# Revit family: 859-001X-001 DN65-300
name_source: partatom
category: Pipe Accessories
units: mm (PartAtom-declared; Revit-internal decimal feet)

## family parameters
Always vertical = Yes
Cut with Voids When Loaded = No
Part Type = Valve - Breaks Into
Round Connector Dimension = Use Diameter
Shared = No
Work Plane-Based = No

## types (41) — shared parameters
10 = 10 mm  [stored 0.0328084 ft]
131 = 131 mm
18 = 11 mm  [stored 0.0360892 ft]
3 = 3 mm  [stored 0.00984252 ft]
48 = 15 mm  [stored 0.0492126 ft]
50 = 50 mm
53 = 20 mm  [stored 0.0656168 ft]
8 = 8 mm  [stored 0.0262467 ft]
DN100_PN10/16_Pilot range ( 0,3 - 1,5) = 859-0100-00-1140018
DN100_PN10/16_Pilot range ( 1,5 - 6) = 859-0100-00-1140010
DN100_PN10/16_Pilot range ( 10 - 16) = 859-0100-00-1140012
DN100_PN10/16_Pilot range ( 5 - 11) = 859-0100-00-1140011
DN125_PN10/16_Pilot range ( 0,3 - 1,5) = 859-0125-00-1140018
DN125_PN10/16_Pilot range ( 1,5 - 6) = 859-0125-00-1140010
DN125_PN10/16_Pilot range ( 10 - 16) = 859-0125-00-1140012
DN125_PN10/16_Pilot range ( 5 - 11) = 859-0125-00-1140011
DN150_PN10/16_Pilot range ( 0,3 - 1,5) = 859-0150-00-1140018
DN150_PN10/16_Pilot range ( 1,5 - 6) = 859-0150-00-1140010
DN150_PN10/16_Pilot range ( 10 - 16) = 859-0150-00-1140012
DN150_PN10/16_Pilot range ( 5 - 11) = 859-0150-00-1140011
DN200_PN10_Pilot range ( 0,3 - 1,5) = 859-0200-00-0140018
DN200_PN10_Pilot range ( 1,5 - 6) = 859-0200-00-0140010
DN200_PN10_Pilot range ( 5 - 10) = 859-0200-00-0140011
DN200_PN16_Pilot range ( 0,3 - 1,5) = 859-0200-00-1140018
DN200_PN16_Pilot range ( 1,5 - 6) = 859-0200-00-1140010
DN200_PN16_Pilot range ( 10 - 16) = 859-0200-00-1140012
DN200_PN16_Pilot range ( 5 - 11) = 859-0200-00-1140011
DN250_PN10_Pilot range ( 0,3 - 1,5) = 859-0250-00-0140018
DN250_PN10_Pilot range ( 1,5 - 6) = 859-0250-00-0140010
DN250_PN10_Pilot range ( 5 - 10) = 859-0250-00-0140011
DN250_PN16_Pilot range ( 0,3 - 1,5) = 859-0250-00-1140018
DN250_PN16_Pilot range ( 1,5 - 6) = 859-0250-00-1140010
DN250_PN16_Pilot range ( 10 - 16) = 859-0250-00-1140012
DN250_PN16_Pilot range ( 5 - 11) = 859-0250-00-1140011
DN300_PN10_Pilot range ( 0,3 - 1,5) = 859-0300-00-0140018
DN300_PN10_Pilot range ( 1,5 - 6) = 859-0300-00-0140010
DN300_PN10_Pilot range ( 5 - 10) = 859-0300-00-0140011
DN300_PN16_Pilot range ( 0,3 - 1,5) = 859-0300-00-1140018
DN300_PN16_Pilot range ( 1,5 - 6) = 859-0300-00-1140010
DN300_PN16_Pilot range ( 10 - 16) = 859-0300-00-1140012
DN300_PN16_Pilot range ( 5 - 11) = 859-0300-00-1140011
DN65_PN10/16_Pilot range ( 0,3 - 1,5) = 859-0065-00-1140018
DN65_PN10/16_Pilot range ( 1,5 - 6) = 859-0065-00-1140010
DN65_PN10/16_Pilot range ( 10 - 16) = 859-0065-00-1140012
DN65_PN10/16_Pilot range ( 5 - 11) = 859-0065-00-1140011
DN80_PN10/16_Pilot range ( 0,3 - 1,5) = 859-0080-00-1140018
DN80_PN10/16_Pilot range ( 1,5 - 6) = 859-0080-00-1140010
DN80_PN10/16_Pilot range ( 10 - 16) = 859-0080-00-1140012
DN80_PN10/16_Pilot range ( 5 - 11) = 859-0080-00-1140011
Description_ = AVK CONTROL VALVE, PRESSURE SUSTAINING/RELIEF, PN10/16
Search_table = 859-001X-001 DN65-300
URL_product_pages = https://www.avkvalves.com
zero-valued in all types: 0, Actuator, Default Elevation

## per-type parameters (varying)
- DN065_PN10/16_Pilot range ( 0,3 - 1,5): Actuator_L=42 mm; Actuator_L1=38 mm; Actuator_d=24 mm  [stored 0.0787402 ft]; Body_H=87 mm; Body_Rib_L=36 mm  [stored 0.11811 ft]; Bolt_Dia=20 mm  [stored 0.0656168 ft]; Bonnet_D=44 mm; Bonnet_D1=87 mm; Bonnet_R=91 mm; Bonnet_dia=94 mm; Bonnet_dim1=61 mm; Bonnet_dim1_H=46 mm; Bonnet_dim1_H1=197 mm; Bonnet_dim2=30 mm  [stored 0.0984252 ft]; Bonnet_dim3=23 mm; Bore=33 mm; Bore1=39 mm  [stored 0.127953 ft]; Bore2=52 mm; Centre_D=25 mm  [stored 0.082021 ft]; Centre_D1=20 mm  [stored 0.0656168 ft]; Centre_nut=19 mm  [stored 0.062336 ft]; Conrol_dim.=52 mm; Control_dim1=9 mm  [stored 0.0295276 ft]; Control_dim2=27 mm; Control_dim3=5 mm  [stored 0.0164042 ft]; Control_dim4=78 mm; Control_dim5=12 mm  [stored 0.0393701 ft]; Control_dim6=15 mm  [stored 0.0492126 ft]; Control_dim7=20 mm  [stored 0.0656168 ft]; D=73 mm; DN=65 mm; FL_T=19 mm  [stored 0.062336 ft]; H3=348 mm; H33=24 mm  [stored 0.0787402 ft]; H4=47 mm; L=290 mm; L3=100 mm; Nut_Dim1=25 mm  [stored 0.082021 ft]; Nut_Dim2=4 mm  [stored 0.0131234 ft]; Nut_T=15 mm  [stored 0.0492126 ft]; Raised_R=16 mm  [stored 0.0524934 ft]; Raised_dis=3 mm  [stored 0.00984252 ft]; Sweep_R=11 mm  [stored 0.0360892 ft]; Thickness=11 mm  [stored 0.0360892 ft]; Thickness1=14 mm  [stored 0.0459318 ft]; W=134 mm; W1=141 mm; W11=101 mm; W2=94 mm; W22=75 mm; Wd1=135 mm; Wd2=135 mm; centre=51 mm; dim1=56 mm; nut_dim=44 mm; sweep=18 mm  [stored 0.0590551 ft]; sweep/2=4 mm  [stored 0.0131234 ft]; sweep1=8 mm  [stored 0.0262467 ft]; sweep_2=4 mm  [stored 0.0131234 ft]; sweep_D=15 mm  [stored 0.0492126 ft]; sweep_H=179 mm; sweep_H1=64 mm; sweep_box1=16 mm  [stored 0.0524934 ft]; sweep_box2=10 mm  [stored 0.0328084 ft]
- DN065_PN10/16_Pilot range ( 1,5 - 6): Actuator_L=42 mm; Actuator_L1=38 mm; Actuator_d=24 mm  [stored 0.0787402 ft]; Body_H=87 mm; Body_Rib_L=36 mm  [stored 0.11811 ft]; Bolt_Dia=20 mm  [stored 0.0656168 ft]; Bonnet_D=44 mm; Bonnet_D1=87 mm; Bonnet_R=91 mm; Bonnet_dia=94 mm; Bonnet_dim1=61 mm; Bonnet_dim1_H=46 mm; Bonnet_dim1_H1=197 mm; Bonnet_dim2=30 mm  [stored 0.0984252 ft]; Bonnet_dim3=23 mm; Bore=33 mm; Bore1=39 mm  [stored 0.127953 ft]; Bore2=52 mm; Centre_D=25 mm  [stored 0.082021 ft]; Centre_D1=20 mm  [stored 0.0656168 ft]; Centre_nut=19 mm  [stored 0.062336 ft]; Conrol_dim.=52 mm; Control_dim1=9 mm  [stored 0.0295276 ft]; Control_dim2=27 mm; Control_dim3=5 mm  [stored 0.0164042 ft]; Control_dim4=78 mm; Control_dim5=12 mm  [stored 0.0393701 ft]; Control_dim6=15 mm  [stored 0.0492126 ft]; Control_dim7=20 mm  [stored 0.0656168 ft]; D=73 mm; DN=65 mm; FL_T=19 mm  [stored 0.062336 ft]; H3=348 mm; H33=24 mm  [stored 0.0787402 ft]; H4=47 mm; L=290 mm; L3=100 mm; Nut_Dim1=25 mm  [stored 0.082021 ft]; Nut_Dim2=4 mm  [stored 0.0131234 ft]; Nut_T=15 mm  [stored 0.0492126 ft]; Raised_R=16 mm  [stored 0.0524934 ft]; Raised_dis=3 mm  [stored 0.00984252 ft]; Sweep_R=11 mm  [stored 0.0360892 ft]; Thickness=11 mm  [stored 0.0360892 ft]; Thickness1=14 mm  [stored 0.0459318 ft]; W=134 mm; W1=141 mm; W11=101 mm; W2=94 mm; W22=75 mm; Wd1=135 mm; Wd2=135 mm; centre=51 mm; dim1=56 mm; nut_dim=44 mm; sweep=18 mm  [stored 0.0590551 ft]; sweep/2=4 mm  [stored 0.0131234 ft]; sweep1=8 mm  [stored 0.0262467 ft]; sweep_2=4 mm  [stored 0.0131234 ft]; sweep_D=15 mm  [stored 0.0492126 ft]; sweep_H=179 mm; sweep_H1=64 mm; sweep_box1=16 mm  [stored 0.0524934 ft]; sweep_box2=10 mm  [stored 0.0328084 ft]
- DN065_PN10/16_Pilot range ( 5 - 11): Actuator_L=42 mm; Actuator_L1=38 mm; Actuator_d=24 mm  [stored 0.0787402 ft]; Body_H=87 mm; Body_Rib_L=36 mm  [stored 0.11811 ft]; Bolt_Dia=20 mm  [stored 0.0656168 ft]; Bonnet_D=44 mm; Bonnet_D1=87 mm; Bonnet_R=91 mm; Bonnet_dia=94 mm; Bonnet_dim1=61 mm; Bonnet_dim1_H=46 mm; Bonnet_dim1_H1=197 mm; Bonnet_dim2=30 mm  [stored 0.0984252 ft]; Bonnet_dim3=23 mm; Bore=33 mm; Bore1=39 mm  [stored 0.127953 ft]; Bore2=52 mm; Centre_D=25 mm  [stored 0.082021 ft]; Centre_D1=20 mm  [stored 0.0656168 ft]; Centre_nut=19 mm  [stored 0.062336 ft]; Conrol_dim.=52 mm; Control_dim1=9 mm  [stored 0.0295276 ft]; Control_dim2=27 mm; Control_dim3=5 mm  [stored 0.0164042 ft]; Control_dim4=78 mm; Control_dim5=12 mm  [stored 0.0393701 ft]; Control_dim6=15 mm  [stored 0.0492126 ft]; Control_dim7=20 mm  [stored 0.0656168 ft]; D=73 mm; DN=65 mm; FL_T=19 mm  [stored 0.062336 ft]; H3=348 mm; H33=24 mm  [stored 0.0787402 ft]; H4=47 mm; L=290 mm; L3=100 mm; Nut_Dim1=25 mm  [stored 0.082021 ft]; Nut_Dim2=4 mm  [stored 0.0131234 ft]; Nut_T=15 mm  [stored 0.0492126 ft]; Raised_R=16 mm  [stored 0.0524934 ft]; Raised_dis=3 mm  [stored 0.00984252 ft]; Sweep_R=11 mm  [stored 0.0360892 ft]; Thickness=11 mm  [stored 0.0360892 ft]; Thickness1=14 mm  [stored 0.0459318 ft]; W=134 mm; W1=141 mm; W11=101 mm; W2=94 mm; W22=75 mm; Wd1=135 mm; Wd2=135 mm; centre=51 mm; dim1=56 mm; nut_dim=44 mm; sweep=18 mm  [stored 0.0590551 ft]; sweep/2=4 mm  [stored 0.0131234 ft]; sweep1=8 mm  [stored 0.0262467 ft]; sweep_2=4 mm  [stored 0.0131234 ft]; sweep_D=15 mm  [stored 0.0492126 ft]; sweep_H=179 mm; sweep_H1=64 mm; sweep_box1=16 mm  [stored 0.0524934 ft]; sweep_box2=10 mm  [stored 0.0328084 ft]
- DN065_PN10/16_Pilot range ( 10 - 16): Actuator_L=42 mm; Actuator_L1=38 mm; Actuator_d=24 mm  [stored 0.0787402 ft]; Body_H=87 mm; Body_Rib_L=36 mm  [stored 0.11811 ft]; Bolt_Dia=20 mm  [stored 0.0656168 ft]; Bonnet_D=44 mm; Bonnet_D1=87 mm; Bonnet_R=91 mm; Bonnet_dia=94 mm; Bonnet_dim1=61 mm; Bonnet_dim1_H=46 mm; Bonnet_dim1_H1=197 mm; Bonnet_dim2=30 mm  [stored 0.0984252 ft]; Bonnet_dim3=23 mm; Bore=33 mm; Bore1=39 mm  [stored 0.127953 ft]; Bore2=52 mm; Centre_D=25 mm  [stored 0.082021 ft]; Centre_D1=20 mm  [stored 0.0656168 ft]; Centre_nut=19 mm  [stored 0.062336 ft]; Conrol_dim.=52 mm; Control_dim1=9 mm  [stored 0.0295276 ft]; Control_dim2=27 mm; Control_dim3=5 mm  [stored 0.0164042 ft]; Control_dim4=78 mm; Control_dim5=12 mm  [stored 0.0393701 ft]; Control_dim6=15 mm  [stored 0.0492126 ft]; Control_dim7=20 mm  [stored 0.0656168 ft]; D=73 mm; DN=65 mm; FL_T=19 mm  [stored 0.062336 ft]; H3=348 mm; H33=24 mm  [stored 0.0787402 ft]; H4=47 mm; L=290 mm; L3=100 mm; Nut_Dim1=25 mm  [stored 0.082021 ft]; Nut_Dim2=4 mm  [stored 0.0131234 ft]; Nut_T=15 mm  [stored 0.0492126 ft]; Raised_R=16 mm  [stored 0.0524934 ft]; Raised_dis=3 mm  [stored 0.00984252 ft]; Sweep_R=11 mm  [stored 0.0360892 ft]; Thickness=11 mm  [stored 0.0360892 ft]; Thickness1=14 mm  [stored 0.0459318 ft]; W=134 mm; W1=141 mm; W11=101 mm; W2=94 mm; W22=75 mm; Wd1=135 mm; Wd2=135 mm; centre=51 mm; dim1=56 mm; nut_dim=44 mm; sweep=18 mm  [stored 0.0590551 ft]; sweep/2=4 mm  [stored 0.0131234 ft]; sweep1=8 mm  [stored 0.0262467 ft]; sweep_2=4 mm  [stored 0.0131234 ft]; sweep_D=15 mm  [stored 0.0492126 ft]; sweep_H=179 mm; sweep_H1=64 mm; sweep_box1=16 mm  [stored 0.0524934 ft]; sweep_box2=10 mm  [stored 0.0328084 ft]
- DN080_PN10/16_Pilot range ( 0,3 - 1,5): Actuator_L=49 mm; Actuator_L1=44 mm; Actuator_d=26 mm; Body_H=96 mm; Body_Rib_L=40 mm  [stored 0.131234 ft]; Bolt_Dia=20 mm  [stored 0.0656168 ft]; Bonnet_D=48 mm; Bonnet_D1=96 mm; Bonnet_R=101 mm; Bonnet_dia=108 mm; Bonnet_dim1=67 mm; Bonnet_dim1_H=45 mm; Bonnet_dim1_H1=205 mm; Bonnet_dim2=34 mm; Bonnet_dim3=25 mm  [stored 0.082021 ft]; Bore=40 mm  [stored 0.131234 ft]; Bore1=48 mm; Bore2=64 mm; Centre_D=25 mm  [stored 0.082021 ft]; Centre_D1=20 mm  [stored 0.0656168 ft]; Centre_nut=19 mm  [stored 0.062336 ft]; Conrol_dim.=57 mm; Control_dim1=10 mm  [stored 0.0328084 ft]; Control_dim2=30 mm  [stored 0.0984252 ft]; Control_dim3=5 mm  [stored 0.0164042 ft]; Control_dim4=86 mm; Control_dim5=14 mm  [stored 0.0459318 ft]; Control_dim6=16 mm  [stored 0.0524934 ft]; Control_dim7=22 mm  [stored 0.0721785 ft]; D=80 mm; DN=80 mm; FL_T=19 mm  [stored 0.062336 ft]; H3=367 mm; H33=25 mm  [stored 0.082021 ft]; H4=49 mm; L=310 mm; L3=111 mm; Nut_Dim1=25 mm  [stored 0.082021 ft]; Nut_Dim2=4 mm  [stored 0.0131234 ft]; Nut_T=15 mm  [stored 0.0492126 ft]; Raised_R=16 mm  [stored 0.0524934 ft]; Raised_dis=3 mm  [stored 0.00984252 ft]; Sweep_R=11 mm  [stored 0.0360892 ft]; Thickness=11 mm  [stored 0.0360892 ft]; Thickness1=14 mm  [stored 0.0459318 ft]; W=134 mm; W1=141 mm; W11=101 mm; W2=108 mm; W22=86 mm; Wd1=135 mm; Wd2=135 mm; centre=62 mm; dim1=56 mm; nut_dim=48 mm; sweep=18 mm  [stored 0.0590551 ft]; sweep/2=4 mm  [stored 0.0131234 ft]; sweep1=8 mm  [stored 0.0262467 ft]; sweep_2=4 mm  [stored 0.0131234 ft]; sweep_D=15 mm  [stored 0.0492126 ft]; sweep_H=187 mm; sweep_H1=63 mm; sweep_box1=16 mm  [stored 0.0524934 ft]; sweep_box2=10 mm  [stored 0.0328084 ft]
- DN080_PN10/16_Pilot range ( 1,5 - 6): Actuator_L=49 mm; Actuator_L1=44 mm; Actuator_d=26 mm; Body_H=96 mm; Body_Rib_L=40 mm  [stored 0.131234 ft]; Bolt_Dia=20 mm  [stored 0.0656168 ft]; Bonnet_D=48 mm; Bonnet_D1=96 mm; Bonnet_R=101 mm; Bonnet_dia=108 mm; Bonnet_dim1=67 mm; Bonnet_dim1_H=45 mm; Bonnet_dim1_H1=205 mm; Bonnet_dim2=34 mm; Bonnet_dim3=25 mm  [stored 0.082021 ft]; Bore=40 mm  [stored 0.131234 ft]; Bore1=48 mm; Bore2=64 mm; Centre_D=25 mm  [stored 0.082021 ft]; Centre_D1=20 mm  [stored 0.0656168 ft]; Centre_nut=19 mm  [stored 0.062336 ft]; Conrol_dim.=57 mm; Control_dim1=10 mm  [stored 0.0328084 ft]; Control_dim2=30 mm  [stored 0.0984252 ft]; Control_dim3=5 mm  [stored 0.0164042 ft]; Control_dim4=86 mm; Control_dim5=14 mm  [stored 0.0459318 ft]; Control_dim6=16 mm  [stored 0.0524934 ft]; Control_dim7=22 mm  [stored 0.0721785 ft]; D=80 mm; DN=80 mm; FL_T=19 mm  [stored 0.062336 ft]; H3=367 mm; H33=25 mm  [stored 0.082021 ft]; H4=49 mm; L=310 mm; L3=111 mm; Nut_Dim1=25 mm  [stored 0.082021 ft]; Nut_Dim2=4 mm  [stored 0.0131234 ft]; Nut_T=15 mm  [stored 0.0492126 ft]; Raised_R=16 mm  [stored 0.0524934 ft]; Raised_dis=3 mm  [stored 0.00984252 ft]; Sweep_R=11 mm  [stored 0.0360892 ft]; Thickness=11 mm  [stored 0.0360892 ft]; Thickness1=14 mm  [stored 0.0459318 ft]; W=134 mm; W1=141 mm; W11=101 mm; W2=108 mm; W22=86 mm; Wd1=135 mm; Wd2=135 mm; centre=63 mm; dim1=56 mm; nut_dim=48 mm; sweep=18 mm  [stored 0.0590551 ft]; sweep/2=4 mm  [stored 0.0131234 ft]; sweep1=8 mm  [stored 0.0262467 ft]; sweep_2=4 mm  [stored 0.0131234 ft]; sweep_D=15 mm  [stored 0.0492126 ft]; sweep_H=187 mm; sweep_H1=63 mm; sweep_box1=16 mm  [stored 0.0524934 ft]; sweep_box2=10 mm  [stored 0.0328084 ft]
- DN080_PN10/16_Pilot range ( 5 - 11): Actuator_L=49 mm; Actuator_L1=44 mm; Actuator_d=26 mm; Body_H=96 mm; Body_Rib_L=40 mm  [stored 0.131234 ft]; Bolt_Dia=20 mm  [stored 0.0656168 ft]; Bonnet_D=48 mm; Bonnet_D1=96 mm; Bonnet_R=101 mm; Bonnet_dia=108 mm; Bonnet_dim1=67 mm; Bonnet_dim1_H=45 mm; Bonnet_dim1_H1=205 mm; Bonnet_dim2=34 mm; Bonnet_dim3=25 mm  [stored 0.082021 ft]; Bore=40 mm  [stored 0.131234 ft]; Bore1=48 mm; Bore2=64 mm; Centre_D=25 mm  [stored 0.082021 ft]; Centre_D1=20 mm  [stored 0.0656168 ft]; Centre_nut=19 mm  [stored 0.062336 ft]; Conrol_dim.=57 mm; Control_dim1=10 mm  [stored 0.0328084 ft]; Control_dim2=30 mm  [stored 0.0984252 ft]; Control_dim3=5 mm  [stored 0.0164042 ft]; Control_dim4=86 mm; Control_dim5=14 mm  [stored 0.0459318 ft]; Control_dim6=16 mm  [stored 0.0524934 ft]; Control_dim7=22 mm  [stored 0.0721785 ft]; D=80 mm; DN=80 mm; FL_T=19 mm  [stored 0.062336 ft]; H3=367 mm; H33=25 mm  [stored 0.082021 ft]; H4=49 mm; L=310 mm; L3=111 mm; Nut_Dim1=25 mm  [stored 0.082021 ft]; Nut_Dim2=4 mm  [stored 0.0131234 ft]; Nut_T=15 mm  [stored 0.0492126 ft]; Raised_R=16 mm  [stored 0.0524934 ft]; Raised_dis=3 mm  [stored 0.00984252 ft]; Sweep_R=11 mm  [stored 0.0360892 ft]; Thickness=11 mm  [stored 0.0360892 ft]; Thickness1=14 mm  [stored 0.0459318 ft]; W=134 mm; W1=141 mm; W11=101 mm; W2=108 mm; W22=86 mm; Wd1=135 mm; Wd2=135 mm; centre=63 mm; dim1=56 mm; nut_dim=48 mm; sweep=18 mm  [stored 0.0590551 ft]; sweep/2=4 mm  [stored 0.0131234 ft]; sweep1=8 mm  [stored 0.0262467 ft]; sweep_2=4 mm  [stored 0.0131234 ft]; sweep_D=15 mm  [stored 0.0492126 ft]; sweep_H=187 mm; sweep_H1=63 mm; sweep_box1=16 mm  [stored 0.0524934 ft]; sweep_box2=10 mm  [stored 0.0328084 ft]
- DN080_PN10/16_Pilot range ( 10 - 16): Actuator_L=49 mm; Actuator_L1=44 mm; Actuator_d=26 mm; Body_H=96 mm; Body_Rib_L=40 mm  [stored 0.131234 ft]; Bolt_Dia=20 mm  [stored 0.0656168 ft]; Bonnet_D=48 mm; Bonnet_D1=96 mm; Bonnet_R=101 mm; Bonnet_dia=108 mm; Bonnet_dim1=67 mm; Bonnet_dim1_H=45 mm; Bonnet_dim1_H1=205 mm; Bonnet_dim2=34 mm; Bonnet_dim3=25 mm  [stored 0.082021 ft]; Bore=40 mm  [stored 0.131234 ft]; Bore1=48 mm; Bore2=64 mm; Centre_D=25 mm  [stored 0.082021 ft]; Centre_D1=20 mm  [stored 0.0656168 ft]; Centre_nut=19 mm  [stored 0.062336 ft]; Conrol_dim.=57 mm; Control_dim1=10 mm  [stored 0.0328084 ft]; Control_dim2=30 mm  [stored 0.0984252 ft]; Control_dim3=5 mm  [stored 0.0164042 ft]; Control_dim4=86 mm; Control_dim5=14 mm  [stored 0.0459318 ft]; Control_dim6=16 mm  [stored 0.0524934 ft]; Control_dim7=22 mm  [stored 0.0721785 ft]; D=80 mm; DN=80 mm; FL_T=19 mm  [stored 0.062336 ft]; H3=367 mm; H33=25 mm  [stored 0.082021 ft]; H4=49 mm; L=310 mm; L3=111 mm; Nut_Dim1=25 mm  [stored 0.082021 ft]; Nut_Dim2=4 mm  [stored 0.0131234 ft]; Nut_T=15 mm  [stored 0.0492126 ft]; Raised_R=16 mm  [stored 0.0524934 ft]; Raised_dis=3 mm  [stored 0.00984252 ft]; Sweep_R=11 mm  [stored 0.0360892 ft]; Thickness=11 mm  [stored 0.0360892 ft]; Thickness1=14 mm  [stored 0.0459318 ft]; W=134 mm; W1=141 mm; W11=101 mm; W2=108 mm; W22=86 mm; Wd1=135 mm; Wd2=135 mm; centre=63 mm; dim1=56 mm; nut_dim=48 mm; sweep=18 mm  [stored 0.0590551 ft]; sweep/2=4 mm  [stored 0.0131234 ft]; sweep1=8 mm  [stored 0.0262467 ft]; sweep_2=4 mm  [stored 0.0131234 ft]; sweep_D=15 mm  [stored 0.0492126 ft]; sweep_H=187 mm; sweep_H1=63 mm; sweep_box1=16 mm  [stored 0.0524934 ft]; sweep_box2=10 mm  [stored 0.0328084 ft]
- DN100_PN10/16_Pilot range ( 0,3 - 1,5): Actuator_L=53 mm; Actuator_L1=48 mm; Actuator_d=30 mm  [stored 0.0984252 ft]; Body_H=108 mm; Body_Rib_L=45 mm; Bolt_Dia=20 mm  [stored 0.0656168 ft]; Bonnet_D=54 mm; Bonnet_D1=108 mm; Bonnet_R=113 mm; Bonnet_dia=117 mm; Bonnet_dim1=76 mm; Bonnet_dim1_H=42 mm; Bonnet_dim1_H1=212 mm; Bonnet_dim2=38 mm; Bonnet_dim3=28 mm; Bore=50 mm; Bore1=60 mm; Bore2=80 mm; Centre_D=30 mm  [stored 0.0984252 ft]; Centre_D1=24 mm  [stored 0.0787402 ft]; Centre_nut=23 mm; Conrol_dim.=64 mm; Control_dim1=11 mm  [stored 0.0360892 ft]; Control_dim2=34 mm; Control_dim3=6 mm  [stored 0.019685 ft]; Control_dim4=97 mm; Control_dim5=15 mm  [stored 0.0492126 ft]; Control_dim6=18 mm  [stored 0.0590551 ft]; Control_dim7=25 mm  [stored 0.082021 ft]; D=90 mm; DN=100 mm; FL_T=19 mm  [stored 0.062336 ft]; H3=386 mm; H33=25 mm  [stored 0.082021 ft]; H4=51 mm; L=350 mm; L3=125 mm; Nut_Dim1=25 mm  [stored 0.082021 ft]; Nut_Dim2=5 mm  [stored 0.0164042 ft]; Nut_T=15 mm  [stored 0.0492126 ft]; Raised_R=16 mm  [stored 0.0524934 ft]; Raised_dis=3 mm  [stored 0.00984252 ft]; Sweep_R=11 mm  [stored 0.0360892 ft]; Thickness=11 mm  [stored 0.0360892 ft]; Thickness1=14 mm  [stored 0.0459318 ft]; W=134 mm; W1=141 mm; W11=101 mm; W2=118 mm; W22=94 mm; Wd1=135 mm; Wd2=138 mm; centre=78 mm; dim1=56 mm; nut_dim=54 mm; sweep=18 mm  [stored 0.0590551 ft]; sweep/2=4 mm  [stored 0.0131234 ft]; sweep1=8 mm  [stored 0.0262467 ft]; sweep_2=4 mm  [stored 0.0131234 ft]; sweep_D=15 mm  [stored 0.0492126 ft]; sweep_H=192 mm; sweep_H1=59 mm; sweep_box1=20 mm  [stored 0.0656168 ft]; sweep_box2=10 mm  [stored 0.0328084 ft]
- DN100_PN10/16_Pilot range ( 1,5 - 6): Actuator_L=53 mm; Actuator_L1=48 mm; Actuator_d=30 mm  [stored 0.0984252 ft]; Body_H=108 mm; Body_Rib_L=45 mm; Bolt_Dia=20 mm  [stored 0.0656168 ft]; Bonnet_D=54 mm; Bonnet_D1=108 mm; Bonnet_R=113 mm; Bonnet_dia=117 mm; Bonnet_dim1=76 mm; Bonnet_dim1_H=42 mm; Bonnet_dim1_H1=212 mm; Bonnet_dim2=38 mm; Bonnet_dim3=28 mm; Bore=50 mm; Bore1=60 mm; Bore2=80 mm; Centre_D=30 mm  [stored 0.0984252 ft]; Centre_D1=24 mm  [stored 0.0787402 ft]; Centre_nut=23 mm; Conrol_dim.=64 mm; Control_dim1=11 mm  [stored 0.0360892 ft]; Control_dim2=34 mm; Control_dim3=6 mm  [stored 0.019685 ft]; Control_dim4=97 mm; Control_dim5=15 mm  [stored 0.0492126 ft]; Control_dim6=18 mm  [stored 0.0590551 ft]; Control_dim7=25 mm  [stored 0.082021 ft]; D=90 mm; DN=100 mm; FL_T=19 mm  [stored 0.062336 ft]; H3=386 mm; H33=25 mm  [stored 0.082021 ft]; H4=51 mm; L=350 mm; L3=125 mm; Nut_Dim1=25 mm  [stored 0.082021 ft]; Nut_Dim2=5 mm  [stored 0.0164042 ft]; Nut_T=15 mm  [stored 0.0492126 ft]; Raised_R=16 mm  [stored 0.0524934 ft]; Raised_dis=3 mm  [stored 0.00984252 ft]; Sweep_R=11 mm  [stored 0.0360892 ft]; Thickness=11 mm  [stored 0.0360892 ft]; Thickness1=14 mm  [stored 0.0459318 ft]; W=134 mm; W1=141 mm; W11=101 mm; W2=118 mm; W22=94 mm; Wd1=135 mm; Wd2=138 mm; centre=78 mm; dim1=56 mm; nut_dim=54 mm; sweep=18 mm  [stored 0.0590551 ft]; sweep/2=4 mm  [stored 0.0131234 ft]; sweep1=8 mm  [stored 0.0262467 ft]; sweep_2=4 mm  [stored 0.0131234 ft]; sweep_D=15 mm  [stored 0.0492126 ft]; sweep_H=192 mm; sweep_H1=59 mm; sweep_box1=20 mm  [stored 0.0656168 ft]; sweep_box2=10 mm  [stored 0.0328084 ft]
- DN100_PN10/16_Pilot range ( 5 - 11): Actuator_L=53 mm; Actuator_L1=48 mm; Actuator_d=30 mm  [stored 0.0984252 ft]; Body_H=108 mm; Body_Rib_L=45 mm; Bolt_Dia=20 mm  [stored 0.0656168 ft]; Bonnet_D=54 mm; Bonnet_D1=108 mm; Bonnet_R=113 mm; Bonnet_dia=117 mm; Bonnet_dim1=76 mm; Bonnet_dim1_H=42 mm; Bonnet_dim1_H1=212 mm; Bonnet_dim2=38 mm; Bonnet_dim3=28 mm; Bore=50 mm; Bore1=60 mm; Bore2=80 mm; Centre_D=30 mm  [stored 0.0984252 ft]; Centre_D1=24 mm  [stored 0.0787402 ft]; Centre_nut=23 mm; Conrol_dim.=64 mm; Control_dim1=11 mm  [stored 0.0360892 ft]; Control_dim2=34 mm; Control_dim3=6 mm  [stored 0.019685 ft]; Control_dim4=97 mm; Control_dim5=15 mm  [stored 0.0492126 ft]; Control_dim6=18 mm  [stored 0.0590551 ft]; Control_dim7=25 mm  [stored 0.082021 ft]; D=90 mm; DN=100 mm; FL_T=19 mm  [stored 0.062336 ft]; H3=386 mm; H33=25 mm  [stored 0.082021 ft]; H4=51 mm; L=350 mm; L3=125 mm; Nut_Dim1=25 mm  [stored 0.082021 ft]; Nut_Dim2=5 mm  [stored 0.0164042 ft]; Nut_T=15 mm  [stored 0.0492126 ft]; Raised_R=16 mm  [stored 0.0524934 ft]; Raised_dis=3 mm  [stored 0.00984252 ft]; Sweep_R=11 mm  [stored 0.0360892 ft]; Thickness=11 mm  [stored 0.0360892 ft]; Thickness1=14 mm  [stored 0.0459318 ft]; W=134 mm; W1=141 mm; W11=101 mm; W2=118 mm; W22=94 mm; Wd1=135 mm; Wd2=138 mm; centre=78 mm; dim1=56 mm; nut_dim=54 mm; sweep=18 mm  [stored 0.0590551 ft]; sweep/2=4 mm  [stored 0.0131234 ft]; sweep1=8 mm  [stored 0.0262467 ft]; sweep_2=4 mm  [stored 0.0131234 ft]; sweep_D=15 mm  [stored 0.0492126 ft]; sweep_H=192 mm; sweep_H1=59 mm; sweep_box1=20 mm  [stored 0.0656168 ft]; sweep_box2=10 mm  [stored 0.0328084 ft]
- DN100_PN10/16_Pilot range ( 10 - 16): Actuator_L=53 mm; Actuator_L1=48 mm; Actuator_d=30 mm  [stored 0.0984252 ft]; Body_H=108 mm; Body_Rib_L=45 mm; Bolt_Dia=20 mm  [stored 0.0656168 ft]; Bonnet_D=54 mm; Bonnet_D1=108 mm; Bonnet_R=113 mm; Bonnet_dia=117 mm; Bonnet_dim1=76 mm; Bonnet_dim1_H=42 mm; Bonnet_dim1_H1=212 mm; Bonnet_dim2=38 mm; Bonnet_dim3=28 mm; Bore=50 mm; Bore1=60 mm; Bore2=80 mm; Centre_D=30 mm  [stored 0.0984252 ft]; Centre_D1=24 mm  [stored 0.0787402 ft]; Centre_nut=23 mm; Conrol_dim.=64 mm; Control_dim1=11 mm  [stored 0.0360892 ft]; Control_dim2=34 mm; Control_dim3=6 mm  [stored 0.019685 ft]; Control_dim4=97 mm; Control_dim5=15 mm  [stored 0.0492126 ft]; Control_dim6=18 mm  [stored 0.0590551 ft]; Control_dim7=25 mm  [stored 0.082021 ft]; D=90 mm; DN=100 mm; FL_T=19 mm  [stored 0.062336 ft]; H3=386 mm; H33=25 mm  [stored 0.082021 ft]; H4=51 mm; L=350 mm; L3=125 mm; Nut_Dim1=25 mm  [stored 0.082021 ft]; Nut_Dim2=5 mm  [stored 0.0164042 ft]; Nut_T=15 mm  [stored 0.0492126 ft]; Raised_R=16 mm  [stored 0.0524934 ft]; Raised_dis=3 mm  [stored 0.00984252 ft]; Sweep_R=11 mm  [stored 0.0360892 ft]; Thickness=11 mm  [stored 0.0360892 ft]; Thickness1=14 mm  [stored 0.0459318 ft]; W=134 mm; W1=141 mm; W11=101 mm; W2=118 mm; W22=94 mm; Wd1=135 mm; Wd2=138 mm; centre=78 mm; dim1=56 mm; nut_dim=54 mm; sweep=18 mm  [stored 0.0590551 ft]; sweep/2=4 mm  [stored 0.0131234 ft]; sweep1=8 mm  [stored 0.0262467 ft]; sweep_2=4 mm  [stored 0.0131234 ft]; sweep_D=15 mm  [stored 0.0492126 ft]; sweep_H=192 mm; sweep_H1=59 mm; sweep_box1=20 mm  [stored 0.0656168 ft]; sweep_box2=10 mm  [stored 0.0328084 ft]
- DN125_PN10/16_Pilot range ( 0,3 - 1,5): Actuator_L=53 mm; Actuator_L1=48 mm; Actuator_d=35 mm  [stored 0.114829 ft]; Body_H=126 mm; Body_Rib_L=53 mm; Bolt_Dia=20 mm  [stored 0.0656168 ft]; Bonnet_D=63 mm; Bonnet_D1=126 mm; Bonnet_R=132 mm; Bonnet_dia=117 mm; Bonnet_dim1=88 mm; Bonnet_dim1_H=35 mm  [stored 0.114829 ft]; Bonnet_dim1_H1=215 mm; Bonnet_dim2=44 mm; Bonnet_dim3=33 mm; Bore=63 mm; Bore1=75 mm; Bore2=100 mm; Centre_D=30 mm  [stored 0.0984252 ft]; Centre_D1=24 mm  [stored 0.0787402 ft]; Centre_nut=23 mm; Conrol_dim.=75 mm; Control_dim1=13 mm  [stored 0.0426509 ft]; Control_dim2=40 mm  [stored 0.131234 ft]; Control_dim3=7 mm  [stored 0.0229659 ft]; Control_dim4=113 mm; Control_dim5=18 mm  [stored 0.0590551 ft]; Control_dim6=21 mm  [stored 0.0688976 ft]; Control_dim7=29 mm; D=105 mm; DN=125 mm; FL_T=19 mm  [stored 0.062336 ft]; H3=405 mm; H33=26 mm; H4=51 mm; L=400 mm; L3=146 mm; Nut_Dim1=25 mm  [stored 0.082021 ft]; Nut_Dim2=5 mm  [stored 0.0164042 ft]; Nut_T=15 mm  [stored 0.0492126 ft]; Raised_R=17 mm; Raised_dis=3 mm  [stored 0.00984252 ft]; Sweep_R=11 mm  [stored 0.0360892 ft]; Thickness=11 mm  [stored 0.0360892 ft]; Thickness1=14 mm  [stored 0.0459318 ft]; W=134 mm; W1=141 mm; W11=101 mm; W2=118 mm; W22=94 mm; Wd1=135 mm; Wd2=148 mm; centre=98 mm; dim1=56 mm; nut_dim=63 mm; sweep=18 mm  [stored 0.0590551 ft]; sweep/2=4 mm  [stored 0.0131234 ft]; sweep1=8 mm  [stored 0.0262467 ft]; sweep_2=4 mm  [stored 0.0131234 ft]; sweep_D=15 mm  [stored 0.0492126 ft]; sweep_H=195 mm; sweep_H1=48 mm; sweep_box1=20 mm  [stored 0.0656168 ft]; sweep_box2=10 mm  [stored 0.0328084 ft]
- DN125_PN10/16_Pilot range ( 1,5 - 6): Actuator_L=53 mm; Actuator_L1=48 mm; Actuator_d=35 mm  [stored 0.114829 ft]; Body_H=126 mm; Body_Rib_L=53 mm; Bolt_Dia=20 mm  [stored 0.0656168 ft]; Bonnet_D=63 mm; Bonnet_D1=126 mm; Bonnet_R=132 mm; Bonnet_dia=117 mm; Bonnet_dim1=88 mm; Bonnet_dim1_H=35 mm  [stored 0.114829 ft]; Bonnet_dim1_H1=215 mm; Bonnet_dim2=44 mm; Bonnet_dim3=33 mm; Bore=63 mm; Bore1=75 mm; Bore2=100 mm; Centre_D=30 mm  [stored 0.0984252 ft]; Centre_D1=24 mm  [stored 0.0787402 ft]; Centre_nut=23 mm; Conrol_dim.=75 mm; Control_dim1=13 mm  [stored 0.0426509 ft]; Control_dim2=40 mm  [stored 0.131234 ft]; Control_dim3=7 mm  [stored 0.0229659 ft]; Control_dim4=113 mm; Control_dim5=18 mm  [stored 0.0590551 ft]; Control_dim6=21 mm  [stored 0.0688976 ft]; Control_dim7=29 mm; D=105 mm; DN=125 mm; FL_T=19 mm  [stored 0.062336 ft]; H3=405 mm; H33=26 mm; H4=51 mm; L=400 mm; L3=146 mm; Nut_Dim1=25 mm  [stored 0.082021 ft]; Nut_Dim2=5 mm  [stored 0.0164042 ft]; Nut_T=15 mm  [stored 0.0492126 ft]; Raised_R=17 mm; Raised_dis=3 mm  [stored 0.00984252 ft]; Sweep_R=11 mm  [stored 0.0360892 ft]; Thickness=11 mm  [stored 0.0360892 ft]; Thickness1=14 mm  [stored 0.0459318 ft]; W=134 mm; W1=141 mm; W11=101 mm; W2=118 mm; W22=94 mm; Wd1=135 mm; Wd2=148 mm; centre=98 mm; dim1=56 mm; nut_dim=63 mm; sweep=18 mm  [stored 0.0590551 ft]; sweep/2=4 mm  [stored 0.0131234 ft]; sweep1=8 mm  [stored 0.0262467 ft]; sweep_2=4 mm  [stored 0.0131234 ft]; sweep_D=15 mm  [stored 0.0492126 ft]; sweep_H=195 mm; sweep_H1=48 mm; sweep_box1=20 mm  [stored 0.0656168 ft]; sweep_box2=10 mm  [stored 0.0328084 ft]
- DN125_PN10/16_Pilot range ( 5 - 11): Actuator_L=53 mm; Actuator_L1=48 mm; Actuator_d=35 mm  [stored 0.114829 ft]; Body_H=126 mm; Body_Rib_L=53 mm; Bolt_Dia=20 mm  [stored 0.0656168 ft]; Bonnet_D=63 mm; Bonnet_D1=126 mm; Bonnet_R=132 mm; Bonnet_dia=117 mm; Bonnet_dim1=88 mm; Bonnet_dim1_H=35 mm  [stored 0.114829 ft]; Bonnet_dim1_H1=215 mm; Bonnet_dim2=44 mm; Bonnet_dim3=33 mm; Bore=63 mm; Bore1=75 mm; Bore2=100 mm; Centre_D=30 mm  [stored 0.0984252 ft]; Centre_D1=24 mm  [stored 0.0787402 ft]; Centre_nut=23 mm; Conrol_dim.=75 mm; Control_dim1=13 mm  [stored 0.0426509 ft]; Control_dim2=40 mm  [stored 0.131234 ft]; Control_dim3=7 mm  [stored 0.0229659 ft]; Control_dim4=113 mm; Control_dim5=18 mm  [stored 0.0590551 ft]; Control_dim6=21 mm  [stored 0.0688976 ft]; Control_dim7=29 mm; D=105 mm; DN=125 mm; FL_T=19 mm  [stored 0.062336 ft]; H3=405 mm; H33=26 mm; H4=51 mm; L=400 mm; L3=146 mm; Nut_Dim1=25 mm  [stored 0.082021 ft]; Nut_Dim2=5 mm  [stored 0.0164042 ft]; Nut_T=15 mm  [stored 0.0492126 ft]; Raised_R=17 mm; Raised_dis=3 mm  [stored 0.00984252 ft]; Sweep_R=11 mm  [stored 0.0360892 ft]; Thickness=11 mm  [stored 0.0360892 ft]; Thickness1=14 mm  [stored 0.0459318 ft]; W=134 mm; W1=141 mm; W11=101 mm; W2=118 mm; W22=94 mm; Wd1=135 mm; Wd2=148 mm; centre=98 mm; dim1=56 mm; nut_dim=63 mm; sweep=18 mm  [stored 0.0590551 ft]; sweep/2=4 mm  [stored 0.0131234 ft]; sweep1=8 mm  [stored 0.0262467 ft]; sweep_2=4 mm  [stored 0.0131234 ft]; sweep_D=15 mm  [stored 0.0492126 ft]; sweep_H=195 mm; sweep_H1=48 mm; sweep_box1=20 mm  [stored 0.0656168 ft]; sweep_box2=10 mm  [stored 0.0328084 ft]
- DN125_PN10/16_Pilot range ( 10 - 16): Actuator_L=53 mm; Actuator_L1=48 mm; Actuator_d=35 mm  [stored 0.114829 ft]; Body_H=126 mm; Body_Rib_L=53 mm; Bolt_Dia=20 mm  [stored 0.0656168 ft]; Bonnet_D=63 mm; Bonnet_D1=126 mm; Bonnet_R=132 mm; Bonnet_dia=117 mm; Bonnet_dim1=88 mm; Bonnet_dim1_H=35 mm  [stored 0.114829 ft]; Bonnet_dim1_H1=215 mm; Bonnet_dim2=44 mm; Bonnet_dim3=33 mm; Bore=63 mm; Bore1=75 mm; Bore2=100 mm; Centre_D=30 mm  [stored 0.0984252 ft]; Centre_D1=24 mm  [stored 0.0787402 ft]; Centre_nut=23 mm; Conrol_dim.=75 mm; Control_dim1=13 mm  [stored 0.0426509 ft]; Control_dim2=40 mm  [stored 0.131234 ft]; Control_dim3=7 mm  [stored 0.0229659 ft]; Control_dim4=113 mm; Control_dim5=18 mm  [stored 0.0590551 ft]; Control_dim6=21 mm  [stored 0.0688976 ft]; Control_dim7=29 mm; D=105 mm; DN=125 mm; FL_T=19 mm  [stored 0.062336 ft]; H3=405 mm; H33=26 mm; H4=51 mm; L=400 mm; L3=146 mm; Nut_Dim1=25 mm  [stored 0.082021 ft]; Nut_Dim2=5 mm  [stored 0.0164042 ft]; Nut_T=15 mm  [stored 0.0492126 ft]; Raised_R=17 mm; Raised_dis=3 mm  [stored 0.00984252 ft]; Sweep_R=11 mm  [stored 0.0360892 ft]; Thickness=11 mm  [stored 0.0360892 ft]; Thickness1=14 mm  [stored 0.0459318 ft]; W=134 mm; W1=141 mm; W11=101 mm; W2=118 mm; W22=94 mm; Wd1=135 mm; Wd2=148 mm; centre=98 mm; dim1=56 mm; nut_dim=63 mm; sweep=18 mm  [stored 0.0590551 ft]; sweep/2=4 mm  [stored 0.0131234 ft]; sweep1=8 mm  [stored 0.0262467 ft]; sweep_2=4 mm  [stored 0.0131234 ft]; sweep_D=15 mm  [stored 0.0492126 ft]; sweep_H=195 mm; sweep_H1=48 mm; sweep_box1=20 mm  [stored 0.0656168 ft]; sweep_box2=10 mm  [stored 0.0328084 ft]
- DN150_PN10/16_Pilot range ( 0,3 - 1,5): Actuator_L=63 mm; Actuator_L1=57 mm; Actuator_d=40 mm  [stored 0.131234 ft]; Body_H=144 mm; Body_Rib_L=60 mm; Bolt_Dia=20 mm  [stored 0.0656168 ft]; Bonnet_D=72 mm; Bonnet_D1=144 mm; Bonnet_R=151 mm; Bonnet_dia=140 mm; Bonnet_dim1=101 mm; Bonnet_dim1_H=33 mm; Bonnet_dim1_H1=231 mm; Bonnet_dim2=50 mm; Bonnet_dim3=38 mm; Bore=75 mm; Bore1=90 mm; Bore2=120 mm; Centre_D=40 mm  [stored 0.131234 ft]; Centre_D1=32 mm  [stored 0.104987 ft]; Centre_nut=30 mm  [stored 0.0984252 ft]; Conrol_dim.=86 mm; Control_dim1=15 mm  [stored 0.0492126 ft]; Control_dim2=45 mm; Control_dim3=8 mm  [stored 0.0262467 ft]; Control_dim4=130 mm; Control_dim5=20 mm  [stored 0.0656168 ft]; Control_dim6=24 mm  [stored 0.0787402 ft]; Control_dim7=33 mm; D=120 mm; DN=150 mm; FL_T=19 mm  [stored 0.062336 ft]; H3=443 mm; H33=28 mm; H4=55 mm; L=480 mm; L3=166 mm; Nut_Dim1=25 mm  [stored 0.082021 ft]; Nut_Dim2=6 mm  [stored 0.019685 ft]; Nut_T=15 mm  [stored 0.0492126 ft]; Raised_R=18 mm  [stored 0.0590551 ft]; Raised_dis=3 mm  [stored 0.00984252 ft]; Sweep_R=11 mm  [stored 0.0360892 ft]; Thickness=11 mm  [stored 0.0360892 ft]; Thickness1=14 mm  [stored 0.0459318 ft]; W=134 mm; W1=141 mm; W11=101 mm; W2=140 mm; W22=112 mm; Wd1=135 mm; Wd2=165 mm; centre=117 mm; dim1=56 mm; nut_dim=72 mm; sweep=18 mm  [stored 0.0590551 ft]; sweep/2=4 mm  [stored 0.0131234 ft]; sweep1=8 mm  [stored 0.0262467 ft]; sweep_2=4 mm  [stored 0.0131234 ft]; sweep_D=15 mm  [stored 0.0492126 ft]; sweep_H=210 mm; sweep_H1=46 mm; sweep_box1=26 mm; sweep_box2=10 mm  [stored 0.0328084 ft]
- DN150_PN10/16_Pilot range ( 1,5 - 6): Actuator_L=63 mm; Actuator_L1=57 mm; Actuator_d=40 mm  [stored 0.131234 ft]; Body_H=144 mm; Body_Rib_L=60 mm; Bolt_Dia=20 mm  [stored 0.0656168 ft]; Bonnet_D=72 mm; Bonnet_D1=144 mm; Bonnet_R=151 mm; Bonnet_dia=140 mm; Bonnet_dim1=101 mm; Bonnet_dim1_H=33 mm; Bonnet_dim1_H1=231 mm; Bonnet_dim2=50 mm; Bonnet_dim3=38 mm; Bore=75 mm; Bore1=90 mm; Bore2=120 mm; Centre_D=40 mm  [stored 0.131234 ft]; Centre_D1=32 mm  [stored 0.104987 ft]; Centre_nut=30 mm  [stored 0.0984252 ft]; Conrol_dim.=86 mm; Control_dim1=15 mm  [stored 0.0492126 ft]; Control_dim2=45 mm; Control_dim3=8 mm  [stored 0.0262467 ft]; Control_dim4=130 mm; Control_dim5=20 mm  [stored 0.0656168 ft]; Control_dim6=24 mm  [stored 0.0787402 ft]; Control_dim7=33 mm; D=120 mm; DN=150 mm; FL_T=19 mm  [stored 0.062336 ft]; H3=443 mm; H33=28 mm; H4=55 mm; L=480 mm; L3=166 mm; Nut_Dim1=25 mm  [stored 0.082021 ft]; Nut_Dim2=6 mm  [stored 0.019685 ft]; Nut_T=15 mm  [stored 0.0492126 ft]; Raised_R=18 mm  [stored 0.0590551 ft]; Raised_dis=3 mm  [stored 0.00984252 ft]; Sweep_R=11 mm  [stored 0.0360892 ft]; Thickness=11 mm  [stored 0.0360892 ft]; Thickness1=14 mm  [stored 0.0459318 ft]; W=134 mm; W1=141 mm; W11=101 mm; W2=140 mm; W22=112 mm; Wd1=135 mm; Wd2=165 mm; centre=117 mm; dim1=56 mm; nut_dim=72 mm; sweep=18 mm  [stored 0.0590551 ft]; sweep/2=4 mm  [stored 0.0131234 ft]; sweep1=8 mm  [stored 0.0262467 ft]; sweep_2=4 mm  [stored 0.0131234 ft]; sweep_D=15 mm  [stored 0.0492126 ft]; sweep_H=210 mm; sweep_H1=46 mm; sweep_box1=26 mm; sweep_box2=10 mm  [stored 0.0328084 ft]
- DN150_PN10/16_Pilot range ( 5 - 11): Actuator_L=63 mm; Actuator_L1=57 mm; Actuator_d=40 mm  [stored 0.131234 ft]; Body_H=144 mm; Body_Rib_L=60 mm; Bolt_Dia=20 mm  [stored 0.0656168 ft]; Bonnet_D=72 mm; Bonnet_D1=144 mm; Bonnet_R=151 mm; Bonnet_dia=140 mm; Bonnet_dim1=101 mm; Bonnet_dim1_H=33 mm; Bonnet_dim1_H1=231 mm; Bonnet_dim2=50 mm; Bonnet_dim3=38 mm; Bore=75 mm; Bore1=90 mm; Bore2=120 mm; Centre_D=40 mm  [stored 0.131234 ft]; Centre_D1=32 mm  [stored 0.104987 ft]; Centre_nut=30 mm  [stored 0.0984252 ft]; Conrol_dim.=86 mm; Control_dim1=15 mm  [stored 0.0492126 ft]; Control_dim2=45 mm; Control_dim3=8 mm  [stored 0.0262467 ft]; Control_dim4=130 mm; Control_dim5=20 mm  [stored 0.0656168 ft]; Control_dim6=24 mm  [stored 0.0787402 ft]; Control_dim7=33 mm; D=120 mm; DN=150 mm; FL_T=19 mm  [stored 0.062336 ft]; H3=443 mm; H33=28 mm; H4=55 mm; L=480 mm; L3=166 mm; Nut_Dim1=25 mm  [stored 0.082021 ft]; Nut_Dim2=6 mm  [stored 0.019685 ft]; Nut_T=15 mm  [stored 0.0492126 ft]; Raised_R=18 mm  [stored 0.0590551 ft]; Raised_dis=3 mm  [stored 0.00984252 ft]; Sweep_R=11 mm  [stored 0.0360892 ft]; Thickness=11 mm  [stored 0.0360892 ft]; Thickness1=14 mm  [stored 0.0459318 ft]; W=134 mm; W1=141 mm; W11=101 mm; W2=140 mm; W22=112 mm; Wd1=135 mm; Wd2=165 mm; centre=117 mm; dim1=56 mm; nut_dim=72 mm; sweep=18 mm  [stored 0.0590551 ft]; sweep/2=4 mm  [stored 0.0131234 ft]; sweep1=8 mm  [stored 0.0262467 ft]; sweep_2=4 mm  [stored 0.0131234 ft]; sweep_D=15 mm  [stored 0.0492126 ft]; sweep_H=210 mm; sweep_H1=46 mm; sweep_box1=26 mm; sweep_box2=10 mm  [stored 0.0328084 ft]
- DN150_PN10/16_Pilot range ( 10 - 16): Actuator_L=63 mm; Actuator_L1=57 mm; Actuator_d=40 mm  [stored 0.131234 ft]; Body_H=144 mm; Body_Rib_L=60 mm; Bolt_Dia=20 mm  [stored 0.0656168 ft]; Bonnet_D=72 mm; Bonnet_D1=144 mm; Bonnet_R=151 mm; Bonnet_dia=140 mm; Bonnet_dim1=101 mm; Bonnet_dim1_H=33 mm; Bonnet_dim1_H1=231 mm; Bonnet_dim2=50 mm; Bonnet_dim3=38 mm; Bore=75 mm; Bore1=90 mm; Bore2=120 mm; Centre_D=40 mm  [stored 0.131234 ft]; Centre_D1=32 mm  [stored 0.104987 ft]; Centre_nut=30 mm  [stored 0.0984252 ft]; Conrol_dim.=86 mm; Control_dim1=15 mm  [stored 0.0492126 ft]; Control_dim2=45 mm; Control_dim3=8 mm  [stored 0.0262467 ft]; Control_dim4=130 mm; Control_dim5=20 mm  [stored 0.0656168 ft]; Control_dim6=24 mm  [stored 0.0787402 ft]; Control_dim7=33 mm; D=120 mm; DN=150 mm; FL_T=19 mm  [stored 0.062336 ft]; H3=443 mm; H33=28 mm; H4=55 mm; L=480 mm; L3=166 mm; Nut_Dim1=25 mm  [stored 0.082021 ft]; Nut_Dim2=6 mm  [stored 0.019685 ft]; Nut_T=15 mm  [stored 0.0492126 ft]; Raised_R=18 mm  [stored 0.0590551 ft]; Raised_dis=3 mm  [stored 0.00984252 ft]; Sweep_R=11 mm  [stored 0.0360892 ft]; Thickness=11 mm  [stored 0.0360892 ft]; Thickness1=14 mm  [stored 0.0459318 ft]; W=134 mm; W1=141 mm; W11=101 mm; W2=140 mm; W22=112 mm; Wd1=135 mm; Wd2=165 mm; centre=117 mm; dim1=56 mm; nut_dim=72 mm; sweep=18 mm  [stored 0.0590551 ft]; sweep/2=4 mm  [stored 0.0131234 ft]; sweep1=8 mm  [stored 0.0262467 ft]; sweep_2=4 mm  [stored 0.0131234 ft]; sweep_D=15 mm  [stored 0.0492126 ft]; sweep_H=210 mm; sweep_H1=46 mm; sweep_box1=26 mm; sweep_box2=10 mm  [stored 0.0328084 ft]
- DN200_PN10_Pilot range ( 0,3 - 1,5): Actuator_L=91 mm; Actuator_L1=82 mm; Actuator_d=49 mm; Body_H=177 mm; Body_Rib_L=74 mm; Bolt_Dia=23 mm; Bonnet_D=89 mm; Bonnet_D1=177 mm; Bonnet_R=186 mm; Bonnet_dia=203 mm; Bonnet_dim1=124 mm; Bonnet_dim1_H=37 mm; Bonnet_dim1_H1=276 mm; Bonnet_dim2=62 mm; Bonnet_dim3=46 mm; Bore=100 mm; Bore1=120 mm; Bore2=160 mm; Centre_D=45 mm; Centre_D1=36 mm  [stored 0.11811 ft]; Centre_nut=34 mm; Conrol_dim.=105 mm; Control_dim1=19 mm  [stored 0.062336 ft]; Control_dim2=56 mm; Control_dim3=9 mm  [stored 0.0295276 ft]; Control_dim4=159 mm; Control_dim5=25 mm  [stored 0.082021 ft]; Control_dim6=30 mm  [stored 0.0984252 ft]; Control_dim7=41 mm; D=148 mm; DN=200 mm; FL_T=20 mm  [stored 0.0656168 ft]; H3=534 mm; H33=33 mm; H4=66 mm; L=600 mm; L3=204 mm; Nut_Dim1=30 mm  [stored 0.0984252 ft]; Nut_Dim2=7 mm  [stored 0.0229659 ft]; Nut_T=16 mm  [stored 0.0524934 ft]; Raised_R=19 mm  [stored 0.062336 ft]; Raised_dis=3 mm  [stored 0.00984252 ft]; Sweep_R=13 mm  [stored 0.0426509 ft]; Thickness=12 mm  [stored 0.0393701 ft]; Thickness1=14 mm  [stored 0.0459318 ft]; W=194 mm; W1=203 mm; W11=148 mm; W2=203 mm; W22=162 mm; Wd1=195 mm; Wd2=203 mm; centre=156 mm; dim1=81 mm; nut_dim=89 mm; sweep=21 mm  [stored 0.0688976 ft]; sweep/2=4 mm  [stored 0.0131234 ft]; sweep1=9 mm  [stored 0.0295276 ft]; sweep_2=4 mm  [stored 0.0131234 ft]; sweep_D=18 mm  [stored 0.0590551 ft]; sweep_H=251 mm; sweep_H1=52 mm; sweep_box1=29 mm; sweep_box2=11 mm  [stored 0.0360892 ft]
- DN200_PN10_Pilot range ( 1,5 - 6): Actuator_L=91 mm; Actuator_L1=82 mm; Actuator_d=49 mm; Body_H=177 mm; Body_Rib_L=74 mm; Bolt_Dia=23 mm; Bonnet_D=89 mm; Bonnet_D1=177 mm; Bonnet_R=186 mm; Bonnet_dia=203 mm; Bonnet_dim1=124 mm; Bonnet_dim1_H=37 mm; Bonnet_dim1_H1=276 mm; Bonnet_dim2=62 mm; Bonnet_dim3=46 mm; Bore=100 mm; Bore1=120 mm; Bore2=160 mm; Centre_D=45 mm; Centre_D1=36 mm  [stored 0.11811 ft]; Centre_nut=34 mm; Conrol_dim.=105 mm; Control_dim1=19 mm  [stored 0.062336 ft]; Control_dim2=56 mm; Control_dim3=9 mm  [stored 0.0295276 ft]; Control_dim4=159 mm; Control_dim5=25 mm  [stored 0.082021 ft]; Control_dim6=30 mm  [stored 0.0984252 ft]; Control_dim7=41 mm; D=148 mm; DN=200 mm; FL_T=20 mm  [stored 0.0656168 ft]; H3=534 mm; H33=33 mm; H4=66 mm; L=600 mm; L3=204 mm; Nut_Dim1=30 mm  [stored 0.0984252 ft]; Nut_Dim2=7 mm  [stored 0.0229659 ft]; Nut_T=16 mm  [stored 0.0524934 ft]; Raised_R=19 mm  [stored 0.062336 ft]; Raised_dis=3 mm  [stored 0.00984252 ft]; Sweep_R=13 mm  [stored 0.0426509 ft]; Thickness=12 mm  [stored 0.0393701 ft]; Thickness1=14 mm  [stored 0.0459318 ft]; W=194 mm; W1=203 mm; W11=148 mm; W2=203 mm; W22=162 mm; Wd1=195 mm; Wd2=203 mm; centre=156 mm; dim1=81 mm; nut_dim=89 mm; sweep=21 mm  [stored 0.0688976 ft]; sweep/2=4 mm  [stored 0.0131234 ft]; sweep1=9 mm  [stored 0.0295276 ft]; sweep_2=4 mm  [stored 0.0131234 ft]; sweep_D=18 mm  [stored 0.0590551 ft]; sweep_H=251 mm; sweep_H1=52 mm; sweep_box1=29 mm; sweep_box2=11 mm  [stored 0.0360892 ft]
- DN200_PN10_Pilot range ( 5 - 10): Actuator_L=91 mm; Actuator_L1=82 mm; Actuator_d=49 mm; Body_H=177 mm; Body_Rib_L=74 mm; Bolt_Dia=23 mm; Bonnet_D=89 mm; Bonnet_D1=177 mm; Bonnet_R=186 mm; Bonnet_dia=203 mm; Bonnet_dim1=124 mm; Bonnet_dim1_H=37 mm; Bonnet_dim1_H1=276 mm; Bonnet_dim2=62 mm; Bonnet_dim3=46 mm; Bore=100 mm; Bore1=120 mm; Bore2=160 mm; Centre_D=45 mm; Centre_D1=36 mm  [stored 0.11811 ft]; Centre_nut=34 mm; Conrol_dim.=105 mm; Control_dim1=19 mm  [stored 0.062336 ft]; Control_dim2=56 mm; Control_dim3=9 mm  [stored 0.0295276 ft]; Control_dim4=159 mm; Control_dim5=25 mm  [stored 0.082021 ft]; Control_dim6=30 mm  [stored 0.0984252 ft]; Control_dim7=41 mm; D=148 mm; DN=200 mm; FL_T=20 mm  [stored 0.0656168 ft]; H3=534 mm; H33=33 mm; H4=66 mm; L=600 mm; L3=204 mm; Nut_Dim1=30 mm  [stored 0.0984252 ft]; Nut_Dim2=7 mm  [stored 0.0229659 ft]; Nut_T=16 mm  [stored 0.0524934 ft]; Raised_R=19 mm  [stored 0.062336 ft]; Raised_dis=3 mm  [stored 0.00984252 ft]; Sweep_R=13 mm  [stored 0.0426509 ft]; Thickness=12 mm  [stored 0.0393701 ft]; Thickness1=14 mm  [stored 0.0459318 ft]; W=194 mm; W1=203 mm; W11=148 mm; W2=203 mm; W22=162 mm; Wd1=195 mm; Wd2=203 mm; centre=156 mm; dim1=81 mm; nut_dim=89 mm; sweep=21 mm  [stored 0.0688976 ft]; sweep/2=4 mm  [stored 0.0131234 ft]; sweep1=9 mm  [stored 0.0295276 ft]; sweep_2=4 mm  [stored 0.0131234 ft]; sweep_D=18 mm  [stored 0.0590551 ft]; sweep_H=251 mm; sweep_H1=52 mm; sweep_box1=29 mm; sweep_box2=11 mm  [stored 0.0360892 ft]
- DN200_PN16_Pilot range ( 0,3 - 1,5): Actuator_L=91 mm; Actuator_L1=82 mm; Actuator_d=49 mm; Body_H=177 mm; Body_Rib_L=74 mm; Bolt_Dia=23 mm; Bonnet_D=89 mm; Bonnet_D1=177 mm; Bonnet_R=186 mm; Bonnet_dia=203 mm; Bonnet_dim1=124 mm; Bonnet_dim1_H=37 mm; Bonnet_dim1_H1=276 mm; Bonnet_dim2=62 mm; Bonnet_dim3=46 mm; Bore=100 mm; Bore1=120 mm; Bore2=160 mm; Centre_D=45 mm; Centre_D1=36 mm  [stored 0.11811 ft]; Centre_nut=34 mm; Conrol_dim.=105 mm; Control_dim1=19 mm  [stored 0.062336 ft]; Control_dim2=56 mm; Control_dim3=9 mm  [stored 0.0295276 ft]; Control_dim4=159 mm; Control_dim5=25 mm  [stored 0.082021 ft]; Control_dim6=30 mm  [stored 0.0984252 ft]; Control_dim7=41 mm; D=148 mm; DN=200 mm; FL_T=20 mm  [stored 0.0656168 ft]; H3=534 mm; H33=33 mm; H4=66 mm; L=600 mm; L3=204 mm; Nut_Dim1=30 mm  [stored 0.0984252 ft]; Nut_Dim2=7 mm  [stored 0.0229659 ft]; Nut_T=16 mm  [stored 0.0524934 ft]; Raised_R=19 mm  [stored 0.062336 ft]; Raised_dis=3 mm  [stored 0.00984252 ft]; Sweep_R=13 mm  [stored 0.0426509 ft]; Thickness=12 mm  [stored 0.0393701 ft]; Thickness1=14 mm  [stored 0.0459318 ft]; W=194 mm; W1=203 mm; W11=148 mm; W2=203 mm; W22=162 mm; Wd1=195 mm; Wd2=203 mm; centre=156 mm; dim1=81 mm; nut_dim=89 mm; sweep=21 mm  [stored 0.0688976 ft]; sweep/2=4 mm  [stored 0.0131234 ft]; sweep1=9 mm  [stored 0.0295276 ft]; sweep_2=4 mm  [stored 0.0131234 ft]; sweep_D=18 mm  [stored 0.0590551 ft]; sweep_H=251 mm; sweep_H1=52 mm; sweep_box1=29 mm; sweep_box2=11 mm  [stored 0.0360892 ft]
- DN200_PN16_Pilot range ( 1,5 - 6): Actuator_L=91 mm; Actuator_L1=82 mm; Actuator_d=49 mm; Body_H=177 mm; Body_Rib_L=74 mm; Bolt_Dia=23 mm; Bonnet_D=89 mm; Bonnet_D1=177 mm; Bonnet_R=186 mm; Bonnet_dia=203 mm; Bonnet_dim1=124 mm; Bonnet_dim1_H=37 mm; Bonnet_dim1_H1=276 mm; Bonnet_dim2=62 mm; Bonnet_dim3=46 mm; Bore=100 mm; Bore1=120 mm; Bore2=160 mm; Centre_D=45 mm; Centre_D1=36 mm  [stored 0.11811 ft]; Centre_nut=34 mm; Conrol_dim.=105 mm; Control_dim1=19 mm  [stored 0.062336 ft]; Control_dim2=56 mm; Control_dim3=9 mm  [stored 0.0295276 ft]; Control_dim4=159 mm; Control_dim5=25 mm  [stored 0.082021 ft]; Control_dim6=30 mm  [stored 0.0984252 ft]; Control_dim7=41 mm; D=148 mm; DN=201 mm; FL_T=20 mm  [stored 0.0656168 ft]; H3=534 mm; H33=33 mm; H4=66 mm; L=600 mm; L3=204 mm; Nut_Dim1=30 mm  [stored 0.0984252 ft]; Nut_Dim2=7 mm  [stored 0.0229659 ft]; Nut_T=16 mm  [stored 0.0524934 ft]; Raised_R=19 mm  [stored 0.062336 ft]; Raised_dis=3 mm  [stored 0.00984252 ft]; Sweep_R=13 mm  [stored 0.0426509 ft]; Thickness=12 mm  [stored 0.0393701 ft]; Thickness1=14 mm  [stored 0.0459318 ft]; W=194 mm; W1=203 mm; W11=148 mm; W2=203 mm; W22=162 mm; Wd1=195 mm; Wd2=203 mm; centre=156 mm; dim1=81 mm; nut_dim=89 mm; sweep=21 mm  [stored 0.0688976 ft]; sweep/2=4 mm  [stored 0.0131234 ft]; sweep1=9 mm  [stored 0.0295276 ft]; sweep_2=4 mm  [stored 0.0131234 ft]; sweep_D=18 mm  [stored 0.0590551 ft]; sweep_H=251 mm; sweep_H1=52 mm; sweep_box1=29 mm; sweep_box2=11 mm  [stored 0.0360892 ft]
- DN200_PN16_Pilot range ( 5 - 11): Actuator_L=91 mm; Actuator_L1=82 mm; Actuator_d=49 mm; Body_H=177 mm; Body_Rib_L=74 mm; Bolt_Dia=23 mm; Bonnet_D=89 mm; Bonnet_D1=177 mm; Bonnet_R=186 mm; Bonnet_dia=203 mm; Bonnet_dim1=124 mm; Bonnet_dim1_H=37 mm; Bonnet_dim1_H1=276 mm; Bonnet_dim2=62 mm; Bonnet_dim3=46 mm; Bore=100 mm; Bore1=120 mm; Bore2=161 mm; Centre_D=45 mm; Centre_D1=36 mm  [stored 0.11811 ft]; Centre_nut=34 mm; Conrol_dim.=105 mm; Control_dim1=19 mm  [stored 0.062336 ft]; Control_dim2=56 mm; Control_dim3=9 mm  [stored 0.0295276 ft]; Control_dim4=159 mm; Control_dim5=25 mm  [stored 0.082021 ft]; Control_dim6=30 mm  [stored 0.0984252 ft]; Control_dim7=41 mm; D=148 mm; DN=201 mm; FL_T=20 mm  [stored 0.0656168 ft]; H3=534 mm; H33=33 mm; H4=66 mm; L=600 mm; L3=204 mm; Nut_Dim1=30 mm  [stored 0.0984252 ft]; Nut_Dim2=7 mm  [stored 0.0229659 ft]; Nut_T=16 mm  [stored 0.0524934 ft]; Raised_R=19 mm  [stored 0.062336 ft]; Raised_dis=3 mm  [stored 0.00984252 ft]; Sweep_R=13 mm  [stored 0.0426509 ft]; Thickness=12 mm  [stored 0.0393701 ft]; Thickness1=14 mm  [stored 0.0459318 ft]; W=194 mm; W1=203 mm; W11=148 mm; W2=203 mm; W22=162 mm; Wd1=195 mm; Wd2=203 mm; centre=157 mm; dim1=81 mm; nut_dim=89 mm; sweep=21 mm  [stored 0.0688976 ft]; sweep/2=4 mm  [stored 0.0131234 ft]; sweep1=9 mm  [stored 0.0295276 ft]; sweep_2=4 mm  [stored 0.0131234 ft]; sweep_D=18 mm  [stored 0.0590551 ft]; sweep_H=251 mm; sweep_H1=52 mm; sweep_box1=29 mm; sweep_box2=11 mm  [stored 0.0360892 ft]
- DN200_PN16_Pilot range ( 10 - 16): Actuator_L=91 mm; Actuator_L1=82 mm; Actuator_d=49 mm; Body_H=177 mm; Body_Rib_L=74 mm; Bolt_Dia=23 mm; Bonnet_D=89 mm; Bonnet_D1=177 mm; Bonnet_R=186 mm; Bonnet_dia=203 mm; Bonnet_dim1=124 mm; Bonnet_dim1_H=37 mm; Bonnet_dim1_H1=276 mm; Bonnet_dim2=62 mm; Bonnet_dim3=46 mm; Bore=100 mm; Bore1=120 mm; Bore2=160 mm; Centre_D=45 mm; Centre_D1=36 mm  [stored 0.11811 ft]; Centre_nut=34 mm; Conrol_dim.=105 mm; Control_dim1=19 mm  [stored 0.062336 ft]; Control_dim2=56 mm; Control_dim3=9 mm  [stored 0.0295276 ft]; Control_dim4=159 mm; Control_dim5=25 mm  [stored 0.082021 ft]; Control_dim6=30 mm  [stored 0.0984252 ft]; Control_dim7=41 mm; D=148 mm; DN=201 mm; FL_T=20 mm  [stored 0.0656168 ft]; H3=534 mm; H33=33 mm; H4=66 mm; L=600 mm; L3=204 mm; Nut_Dim1=30 mm  [stored 0.0984252 ft]; Nut_Dim2=7 mm  [stored 0.0229659 ft]; Nut_T=16 mm  [stored 0.0524934 ft]; Raised_R=19 mm  [stored 0.062336 ft]; Raised_dis=3 mm  [stored 0.00984252 ft]; Sweep_R=13 mm  [stored 0.0426509 ft]; Thickness=12 mm  [stored 0.0393701 ft]; Thickness1=14 mm  [stored 0.0459318 ft]; W=194 mm; W1=203 mm; W11=148 mm; W2=203 mm; W22=162 mm; Wd1=195 mm; Wd2=203 mm; centre=156 mm; dim1=81 mm; nut_dim=89 mm; sweep=21 mm  [stored 0.0688976 ft]; sweep/2=4 mm  [stored 0.0131234 ft]; sweep1=9 mm  [stored 0.0295276 ft]; sweep_2=4 mm  [stored 0.0131234 ft]; sweep_D=18 mm  [stored 0.0590551 ft]; sweep_H=251 mm; sweep_H1=52 mm; sweep_box1=29 mm; sweep_box2=11 mm  [stored 0.0360892 ft]
- DN250_PN10_Pilot range ( 0,3 - 1,5): Actuator_L=114 mm; Actuator_L1=103 mm; Actuator_d=59 mm; Body_H=213 mm; Body_Rib_L=89 mm; Bolt_Dia=26 mm; Bonnet_D=107 mm; Bonnet_D1=213 mm; Bonnet_R=224 mm; Bonnet_dia=254 mm; Bonnet_dim1=149 mm; Bonnet_dim1_H=47 mm; Bonnet_dim1_H1=339 mm; Bonnet_dim2=75 mm; Bonnet_dim3=56 mm; Bore=125 mm; Bore1=150 mm; Bore2=200 mm; Centre_D=50 mm; Centre_D1=40 mm  [stored 0.131234 ft]; Centre_nut=38 mm; Conrol_dim.=127 mm; Control_dim1=22 mm  [stored 0.0721785 ft]; Control_dim2=67 mm; Control_dim3=11 mm  [stored 0.0360892 ft]; Control_dim4=192 mm; Control_dim5=30 mm  [stored 0.0984252 ft]; Control_dim6=36 mm  [stored 0.11811 ft]; Control_dim7=49 mm; D=178 mm; DN=250 mm; FL_T=22 mm  [stored 0.0721785 ft]; H3=651 mm; H33=40 mm  [stored 0.131234 ft]; H4=81 mm; L=730 mm; L3=246 mm; Nut_Dim1=34 mm; Nut_Dim2=9 mm  [stored 0.0295276 ft]; Nut_T=18 mm  [stored 0.0590551 ft]; Raised_R=21 mm  [stored 0.0688976 ft]; Raised_dis=3 mm  [stored 0.00984252 ft]; Sweep_R=15 mm  [stored 0.0492126 ft]; Thickness=13 mm  [stored 0.0426509 ft]; Thickness1=16 mm  [stored 0.0524934 ft]; W=244 mm; W1=254 mm; W11=187 mm; W2=254 mm; W22=203 mm; Wd1=244 mm; Wd2=254 mm; centre=195 mm; dim1=102 mm; nut_dim=107 mm; sweep=24 mm  [stored 0.0787402 ft]; sweep/2=5 mm  [stored 0.0164042 ft]; sweep1=10 mm  [stored 0.0328084 ft]; sweep_2=5 mm  [stored 0.0164042 ft]; sweep_D=20 mm  [stored 0.0656168 ft]; sweep_H=308 mm; sweep_H1=66 mm; sweep_box1=33 mm; sweep_box2=13 mm  [stored 0.0426509 ft]
- DN250_PN10_Pilot range ( 5 - 10): Actuator_L=114 mm; Actuator_L1=103 mm; Actuator_d=59 mm; Body_H=213 mm; Body_Rib_L=89 mm; Bolt_Dia=26 mm; Bonnet_D=107 mm; Bonnet_D1=213 mm; Bonnet_R=224 mm; Bonnet_dia=254 mm; Bonnet_dim1=149 mm; Bonnet_dim1_H=47 mm; Bonnet_dim1_H1=339 mm; Bonnet_dim2=75 mm; Bonnet_dim3=56 mm; Bore=125 mm; Bore1=150 mm; Bore2=200 mm; Centre_D=50 mm; Centre_D1=40 mm  [stored 0.131234 ft]; Centre_nut=38 mm; Conrol_dim.=127 mm; Control_dim1=22 mm  [stored 0.0721785 ft]; Control_dim2=67 mm; Control_dim3=11 mm  [stored 0.0360892 ft]; Control_dim4=192 mm; Control_dim5=30 mm  [stored 0.0984252 ft]; Control_dim6=36 mm  [stored 0.11811 ft]; Control_dim7=49 mm; D=178 mm; DN=250 mm; FL_T=22 mm  [stored 0.0721785 ft]; H3=651 mm; H33=40 mm  [stored 0.131234 ft]; H4=81 mm; L=730 mm; L3=246 mm; Nut_Dim1=34 mm; Nut_Dim2=9 mm  [stored 0.0295276 ft]; Nut_T=18 mm  [stored 0.0590551 ft]; Raised_R=21 mm  [stored 0.0688976 ft]; Raised_dis=3 mm  [stored 0.00984252 ft]; Sweep_R=15 mm  [stored 0.0492126 ft]; Thickness=13 mm  [stored 0.0426509 ft]; Thickness1=16 mm  [stored 0.0524934 ft]; W=244 mm; W1=254 mm; W11=187 mm; W2=254 mm; W22=203 mm; Wd1=244 mm; Wd2=254 mm; centre=195 mm; dim1=102 mm; nut_dim=107 mm; sweep=24 mm  [stored 0.0787402 ft]; sweep/2=5 mm  [stored 0.0164042 ft]; sweep1=10 mm  [stored 0.0328084 ft]; sweep_2=5 mm  [stored 0.0164042 ft]; sweep_D=20 mm  [stored 0.0656168 ft]; sweep_H=308 mm; sweep_H1=66 mm; sweep_box1=33 mm; sweep_box2=13 mm  [stored 0.0426509 ft]
- DN250_PN10_Pilot range ( 1,5 - 6): Actuator_L=114 mm; Actuator_L1=103 mm; Actuator_d=59 mm; Body_H=213 mm; Body_Rib_L=89 mm; Bolt_Dia=26 mm; Bonnet_D=107 mm; Bonnet_D1=213 mm; Bonnet_R=224 mm; Bonnet_dia=254 mm; Bonnet_dim1=149 mm; Bonnet_dim1_H=47 mm; Bonnet_dim1_H1=339 mm; Bonnet_dim2=75 mm; Bonnet_dim3=56 mm; Bore=125 mm; Bore1=150 mm; Bore2=200 mm; Centre_D=50 mm; Centre_D1=40 mm  [stored 0.131234 ft]; Centre_nut=38 mm; Conrol_dim.=127 mm; Control_dim1=22 mm  [stored 0.0721785 ft]; Control_dim2=67 mm; Control_dim3=11 mm  [stored 0.0360892 ft]; Control_dim4=192 mm; Control_dim5=30 mm  [stored 0.0984252 ft]; Control_dim6=36 mm  [stored 0.11811 ft]; Control_dim7=49 mm; D=178 mm; DN=250 mm; FL_T=22 mm  [stored 0.0721785 ft]; H3=651 mm; H33=40 mm  [stored 0.131234 ft]; H4=81 mm; L=730 mm; L3=246 mm; Nut_Dim1=34 mm; Nut_Dim2=9 mm  [stored 0.0295276 ft]; Nut_T=18 mm  [stored 0.0590551 ft]; Raised_R=21 mm  [stored 0.0688976 ft]; Raised_dis=3 mm  [stored 0.00984252 ft]; Sweep_R=15 mm  [stored 0.0492126 ft]; Thickness=13 mm  [stored 0.0426509 ft]; Thickness1=16 mm  [stored 0.0524934 ft]; W=244 mm; W1=254 mm; W11=187 mm; W2=254 mm; W22=203 mm; Wd1=244 mm; Wd2=254 mm; centre=195 mm; dim1=102 mm; nut_dim=107 mm; sweep=24 mm  [stored 0.0787402 ft]; sweep/2=5 mm  [stored 0.0164042 ft]; sweep1=10 mm  [stored 0.0328084 ft]; sweep_2=5 mm  [stored 0.0164042 ft]; sweep_D=20 mm  [stored 0.0656168 ft]; sweep_H=308 mm; sweep_H1=66 mm; sweep_box1=33 mm; sweep_box2=13 mm  [stored 0.0426509 ft]
- DN250_PN16_Pilot range ( 0,3 - 1,5): Actuator_L=114 mm; Actuator_L1=103 mm; Actuator_d=59 mm; Body_H=213 mm; Body_Rib_L=89 mm; Bolt_Dia=26 mm; Bonnet_D=107 mm; Bonnet_D1=213 mm; Bonnet_R=224 mm; Bonnet_dia=254 mm; Bonnet_dim1=149 mm; Bonnet_dim1_H=47 mm; Bonnet_dim1_H1=339 mm; Bonnet_dim2=75 mm; Bonnet_dim3=56 mm; Bore=125 mm; Bore1=150 mm; Bore2=200 mm; Centre_D=50 mm; Centre_D1=40 mm  [stored 0.131234 ft]; Centre_nut=38 mm; Conrol_dim.=127 mm; Control_dim1=22 mm  [stored 0.0721785 ft]; Control_dim2=67 mm; Control_dim3=11 mm  [stored 0.0360892 ft]; Control_dim4=192 mm; Control_dim5=30 mm  [stored 0.0984252 ft]; Control_dim6=36 mm  [stored 0.11811 ft]; Control_dim7=49 mm; D=178 mm; DN=250 mm; FL_T=22 mm  [stored 0.0721785 ft]; H3=651 mm; H33=40 mm  [stored 0.131234 ft]; H4=81 mm; L=730 mm; L3=246 mm; Nut_Dim1=34 mm; Nut_Dim2=9 mm  [stored 0.0295276 ft]; Nut_T=18 mm  [stored 0.0590551 ft]; Raised_R=21 mm  [stored 0.0688976 ft]; Raised_dis=3 mm  [stored 0.00984252 ft]; Sweep_R=15 mm  [stored 0.0492126 ft]; Thickness=13 mm  [stored 0.0426509 ft]; Thickness1=16 mm  [stored 0.0524934 ft]; W=244 mm; W1=254 mm; W11=187 mm; W2=254 mm; W22=203 mm; Wd1=244 mm; Wd2=254 mm; centre=195 mm; dim1=102 mm; nut_dim=107 mm; sweep=24 mm  [stored 0.0787402 ft]; sweep/2=5 mm  [stored 0.0164042 ft]; sweep1=10 mm  [stored 0.0328084 ft]; sweep_2=5 mm  [stored 0.0164042 ft]; sweep_D=20 mm  [stored 0.0656168 ft]; sweep_H=308 mm; sweep_H1=66 mm; sweep_box1=33 mm; sweep_box2=13 mm  [stored 0.0426509 ft]
- DN250_PN16_Pilot range ( 5 - 11): Actuator_L=114 mm; Actuator_L1=103 mm; Actuator_d=59 mm; Body_H=213 mm; Body_Rib_L=89 mm; Bolt_Dia=26 mm; Bonnet_D=107 mm; Bonnet_D1=213 mm; Bonnet_R=224 mm; Bonnet_dia=254 mm; Bonnet_dim1=149 mm; Bonnet_dim1_H=47 mm; Bonnet_dim1_H1=339 mm; Bonnet_dim2=75 mm; Bonnet_dim3=56 mm; Bore=125 mm; Bore1=150 mm; Bore2=200 mm; Centre_D=50 mm; Centre_D1=40 mm  [stored 0.131234 ft]; Centre_nut=38 mm; Conrol_dim.=127 mm; Control_dim1=22 mm  [stored 0.0721785 ft]; Control_dim2=67 mm; Control_dim3=11 mm  [stored 0.0360892 ft]; Control_dim4=192 mm; Control_dim5=30 mm  [stored 0.0984252 ft]; Control_dim6=36 mm  [stored 0.11811 ft]; Control_dim7=49 mm; D=178 mm; DN=251 mm; FL_T=22 mm  [stored 0.0721785 ft]; H3=651 mm; H33=40 mm  [stored 0.131234 ft]; H4=81 mm; L=730 mm; L3=246 mm; Nut_Dim1=34 mm; Nut_Dim2=9 mm  [stored 0.0295276 ft]; Nut_T=18 mm  [stored 0.0590551 ft]; Raised_R=21 mm  [stored 0.0688976 ft]; Raised_dis=3 mm  [stored 0.00984252 ft]; Sweep_R=15 mm  [stored 0.0492126 ft]; Thickness=13 mm  [stored 0.0426509 ft]; Thickness1=16 mm  [stored 0.0524934 ft]; W=244 mm; W1=254 mm; W11=187 mm; W2=254 mm; W22=203 mm; Wd1=244 mm; Wd2=254 mm; centre=195 mm; dim1=102 mm; nut_dim=107 mm; sweep=24 mm  [stored 0.0787402 ft]; sweep/2=5 mm  [stored 0.0164042 ft]; sweep1=10 mm  [stored 0.0328084 ft]; sweep_2=5 mm  [stored 0.0164042 ft]; sweep_D=20 mm  [stored 0.0656168 ft]; sweep_H=308 mm; sweep_H1=66 mm; sweep_box1=33 mm; sweep_box2=13 mm  [stored 0.0426509 ft]
- DN250_PN16_Pilot range ( 10 - 16): Actuator_L=114 mm; Actuator_L1=103 mm; Actuator_d=59 mm; Body_H=213 mm; Body_Rib_L=89 mm; Bolt_Dia=26 mm; Bonnet_D=107 mm; Bonnet_D1=213 mm; Bonnet_R=224 mm; Bonnet_dia=254 mm; Bonnet_dim1=149 mm; Bonnet_dim1_H=47 mm; Bonnet_dim1_H1=339 mm; Bonnet_dim2=75 mm; Bonnet_dim3=56 mm; Bore=125 mm; Bore1=150 mm; Bore2=200 mm; Centre_D=50 mm; Centre_D1=40 mm  [stored 0.131234 ft]; Centre_nut=38 mm; Conrol_dim.=127 mm; Control_dim1=22 mm  [stored 0.0721785 ft]; Control_dim2=67 mm; Control_dim3=11 mm  [stored 0.0360892 ft]; Control_dim4=192 mm; Control_dim5=30 mm  [stored 0.0984252 ft]; Control_dim6=36 mm  [stored 0.11811 ft]; Control_dim7=49 mm; D=178 mm; DN=251 mm; FL_T=22 mm  [stored 0.0721785 ft]; H3=651 mm; H33=40 mm  [stored 0.131234 ft]; H4=81 mm; L=730 mm; L3=246 mm; Nut_Dim1=34 mm; Nut_Dim2=9 mm  [stored 0.0295276 ft]; Nut_T=18 mm  [stored 0.0590551 ft]; Raised_R=21 mm  [stored 0.0688976 ft]; Raised_dis=3 mm  [stored 0.00984252 ft]; Sweep_R=15 mm  [stored 0.0492126 ft]; Thickness=13 mm  [stored 0.0426509 ft]; Thickness1=16 mm  [stored 0.0524934 ft]; W=244 mm; W1=254 mm; W11=187 mm; W2=254 mm; W22=203 mm; Wd1=244 mm; Wd2=254 mm; centre=195 mm; dim1=102 mm; nut_dim=107 mm; sweep=24 mm  [stored 0.0787402 ft]; sweep/2=5 mm  [stored 0.0164042 ft]; sweep1=10 mm  [stored 0.0328084 ft]; sweep_2=5 mm  [stored 0.0164042 ft]; sweep_D=20 mm  [stored 0.0656168 ft]; sweep_H=308 mm; sweep_H1=66 mm; sweep_box1=33 mm; sweep_box2=13 mm  [stored 0.0426509 ft]
- DN250_PN16_Pilot range ( 1,5 - 6): Actuator_L=114 mm; Actuator_L1=103 mm; Actuator_d=59 mm; Body_H=213 mm; Body_Rib_L=89 mm; Bolt_Dia=26 mm; Bonnet_D=107 mm; Bonnet_D1=213 mm; Bonnet_R=224 mm; Bonnet_dia=254 mm; Bonnet_dim1=149 mm; Bonnet_dim1_H=47 mm; Bonnet_dim1_H1=339 mm; Bonnet_dim2=75 mm; Bonnet_dim3=56 mm; Bore=125 mm; Bore1=150 mm; Bore2=200 mm; Centre_D=50 mm; Centre_D1=40 mm  [stored 0.131234 ft]; Centre_nut=38 mm; Conrol_dim.=127 mm; Control_dim1=22 mm  [stored 0.0721785 ft]; Control_dim2=67 mm; Control_dim3=11 mm  [stored 0.0360892 ft]; Control_dim4=192 mm; Control_dim5=30 mm  [stored 0.0984252 ft]; Control_dim6=36 mm  [stored 0.11811 ft]; Control_dim7=49 mm; D=178 mm; DN=251 mm; FL_T=22 mm  [stored 0.0721785 ft]; H3=651 mm; H33=40 mm  [stored 0.131234 ft]; H4=81 mm; L=730 mm; L3=246 mm; Nut_Dim1=34 mm; Nut_Dim2=9 mm  [stored 0.0295276 ft]; Nut_T=18 mm  [stored 0.0590551 ft]; Raised_R=21 mm  [stored 0.0688976 ft]; Raised_dis=3 mm  [stored 0.00984252 ft]; Sweep_R=15 mm  [stored 0.0492126 ft]; Thickness=13 mm  [stored 0.0426509 ft]; Thickness1=16 mm  [stored 0.0524934 ft]; W=244 mm; W1=254 mm; W11=187 mm; W2=254 mm; W22=203 mm; Wd1=244 mm; Wd2=254 mm; centre=195 mm; dim1=102 mm; nut_dim=107 mm; sweep=24 mm  [stored 0.0787402 ft]; sweep/2=5 mm  [stored 0.0164042 ft]; sweep1=10 mm  [stored 0.0328084 ft]; sweep_2=5 mm  [stored 0.0164042 ft]; sweep_D=20 mm  [stored 0.0656168 ft]; sweep_H=308 mm; sweep_H1=66 mm; sweep_box1=33 mm; sweep_box2=13 mm  [stored 0.0426509 ft]
- DN300_PN10_Pilot range ( 0,3 - 1,5): Actuator_L=125 mm; Actuator_L1=112 mm; Actuator_d=68 mm; Body_H=246 mm; Body_Rib_L=103 mm; Bolt_Dia=33 mm; Bonnet_D=123 mm; Bonnet_D1=246 mm; Bonnet_R=258 mm; Bonnet_dia=277 mm; Bonnet_dim1=172 mm; Bonnet_dim1_H=47 mm; Bonnet_dim1_H1=374 mm; Bonnet_dim2=86 mm; Bonnet_dim3=65 mm; Bore=150 mm; Bore1=180 mm; Bore2=240 mm; Centre_D=60 mm; Centre_D1=48 mm; Centre_nut=45 mm; Conrol_dim.=146 mm; Control_dim1=26 mm; Control_dim2=77 mm; Control_dim3=13 mm  [stored 0.0426509 ft]; Control_dim4=221 mm; Control_dim5=35 mm  [stored 0.114829 ft]; Control_dim6=42 mm; Control_dim7=56 mm; D=205 mm; DN=300 mm; FL_T=25 mm  [stored 0.082021 ft]; H3=728 mm; H33=45 mm; H4=89 mm; L=850 mm; L3=284 mm; Nut_Dim1=42 mm; Nut_Dim2=10 mm  [stored 0.0328084 ft]; Nut_T=20 mm  [stored 0.0656168 ft]; Raised_R=22 mm  [stored 0.0721785 ft]; Raised_dis=4 mm  [stored 0.0131234 ft]; Sweep_R=19 mm  [stored 0.062336 ft]; Thickness=15 mm  [stored 0.0492126 ft]; Thickness1=18 mm  [stored 0.0590551 ft]; W=265 mm; W1=277 mm; W11=202 mm; W2=277 mm; W22=222 mm; Wd1=266 mm; Wd2=277 mm; centre=234 mm; dim1=111 mm; nut_dim=123 mm; sweep=30 mm  [stored 0.0984252 ft]; sweep/2=6 mm  [stored 0.019685 ft]; sweep1=13 mm  [stored 0.0426509 ft]; sweep_2=6 mm  [stored 0.019685 ft]; sweep_D=25 mm  [stored 0.082021 ft]; sweep_H=340 mm; sweep_H1=66 mm; sweep_box1=39 mm  [stored 0.127953 ft]; sweep_box2=16 mm  [stored 0.0524934 ft]
- DN300_PN10_Pilot range ( 1,5 - 6): Actuator_L=125 mm; Actuator_L1=112 mm; Actuator_d=68 mm; Body_H=246 mm; Body_Rib_L=103 mm; Bolt_Dia=33 mm; Bonnet_D=123 mm; Bonnet_D1=246 mm; Bonnet_R=258 mm; Bonnet_dia=277 mm; Bonnet_dim1=172 mm; Bonnet_dim1_H=47 mm; Bonnet_dim1_H1=374 mm; Bonnet_dim2=86 mm; Bonnet_dim3=65 mm; Bore=150 mm; Bore1=180 mm; Bore2=240 mm; Centre_D=60 mm; Centre_D1=48 mm; Centre_nut=45 mm; Conrol_dim.=146 mm; Control_dim1=26 mm; Control_dim2=77 mm; Control_dim3=13 mm  [stored 0.0426509 ft]; Control_dim4=221 mm; Control_dim5=35 mm  [stored 0.114829 ft]; Control_dim6=42 mm; Control_dim7=56 mm; D=205 mm; DN=300 mm; FL_T=25 mm  [stored 0.082021 ft]; H3=728 mm; H33=45 mm; H4=89 mm; L=850 mm; L3=284 mm; Nut_Dim1=42 mm; Nut_Dim2=10 mm  [stored 0.0328084 ft]; Nut_T=20 mm  [stored 0.0656168 ft]; Raised_R=22 mm  [stored 0.0721785 ft]; Raised_dis=4 mm  [stored 0.0131234 ft]; Sweep_R=19 mm  [stored 0.062336 ft]; Thickness=15 mm  [stored 0.0492126 ft]; Thickness1=18 mm  [stored 0.0590551 ft]; W=265 mm; W1=277 mm; W11=202 mm; W2=277 mm; W22=222 mm; Wd1=266 mm; Wd2=277 mm; centre=234 mm; dim1=111 mm; nut_dim=123 mm; sweep=30 mm  [stored 0.0984252 ft]; sweep/2=6 mm  [stored 0.019685 ft]; sweep1=13 mm  [stored 0.0426509 ft]; sweep_2=6 mm  [stored 0.019685 ft]; sweep_D=25 mm  [stored 0.082021 ft]; sweep_H=340 mm; sweep_H1=66 mm; sweep_box1=39 mm  [stored 0.127953 ft]; sweep_box2=16 mm  [stored 0.0524934 ft]
- DN300_PN10_Pilot range ( 5 - 10): Actuator_L=125 mm; Actuator_L1=112 mm; Actuator_d=68 mm; Body_H=246 mm; Body_Rib_L=103 mm; Bolt_Dia=33 mm; Bonnet_D=123 mm; Bonnet_D1=246 mm; Bonnet_R=258 mm; Bonnet_dia=277 mm; Bonnet_dim1=172 mm; Bonnet_dim1_H=47 mm; Bonnet_dim1_H1=374 mm; Bonnet_dim2=86 mm; Bonnet_dim3=65 mm; Bore=150 mm; Bore1=180 mm; Bore2=240 mm; Centre_D=60 mm; Centre_D1=48 mm; Centre_nut=45 mm; Conrol_dim.=146 mm; Control_dim1=26 mm; Control_dim2=77 mm; Control_dim3=13 mm  [stored 0.0426509 ft]; Control_dim4=221 mm; Control_dim5=35 mm  [stored 0.114829 ft]; Control_dim6=42 mm; Control_dim7=56 mm; D=205 mm; DN=300 mm; FL_T=25 mm  [stored 0.082021 ft]; H3=728 mm; H33=45 mm; H4=89 mm; L=850 mm; L3=284 mm; Nut_Dim1=42 mm; Nut_Dim2=10 mm  [stored 0.0328084 ft]; Nut_T=20 mm  [stored 0.0656168 ft]; Raised_R=22 mm  [stored 0.0721785 ft]; Raised_dis=4 mm  [stored 0.0131234 ft]; Sweep_R=19 mm  [stored 0.062336 ft]; Thickness=15 mm  [stored 0.0492126 ft]; Thickness1=18 mm  [stored 0.0590551 ft]; W=265 mm; W1=277 mm; W11=202 mm; W2=277 mm; W22=222 mm; Wd1=266 mm; Wd2=277 mm; centre=234 mm; dim1=111 mm; nut_dim=123 mm; sweep=30 mm  [stored 0.0984252 ft]; sweep/2=6 mm  [stored 0.019685 ft]; sweep1=13 mm  [stored 0.0426509 ft]; sweep_2=6 mm  [stored 0.019685 ft]; sweep_D=25 mm  [stored 0.082021 ft]; sweep_H=340 mm; sweep_H1=66 mm; sweep_box1=39 mm  [stored 0.127953 ft]; sweep_box2=16 mm  [stored 0.0524934 ft]
- DN300_PN16_Pilot range ( 0,3 - 1,5): Actuator_L=125 mm; Actuator_L1=112 mm; Actuator_d=68 mm; Body_H=246 mm; Body_Rib_L=103 mm; Bolt_Dia=33 mm; Bonnet_D=123 mm; Bonnet_D1=246 mm; Bonnet_R=258 mm; Bonnet_dia=277 mm; Bonnet_dim1=172 mm; Bonnet_dim1_H=47 mm; Bonnet_dim1_H1=374 mm; Bonnet_dim2=86 mm; Bonnet_dim3=65 mm; Bore=150 mm; Bore1=180 mm; Bore2=240 mm; Centre_D=60 mm; Centre_D1=48 mm; Centre_nut=45 mm; Conrol_dim.=146 mm; Control_dim1=26 mm; Control_dim2=77 mm; Control_dim3=13 mm  [stored 0.0426509 ft]; Control_dim4=221 mm; Control_dim5=35 mm  [stored 0.114829 ft]; Control_dim6=42 mm; Control_dim7=56 mm; D=205 mm; DN=300 mm; FL_T=25 mm  [stored 0.082021 ft]; H3=728 mm; H33=45 mm; H4=89 mm; L=850 mm; L3=284 mm; Nut_Dim1=42 mm; Nut_Dim2=10 mm  [stored 0.0328084 ft]; Nut_T=20 mm  [stored 0.0656168 ft]; Raised_R=22 mm  [stored 0.0721785 ft]; Raised_dis=4 mm  [stored 0.0131234 ft]; Sweep_R=19 mm  [stored 0.062336 ft]; Thickness=15 mm  [stored 0.0492126 ft]; Thickness1=18 mm  [stored 0.0590551 ft]; W=265 mm; W1=277 mm; W11=202 mm; W2=277 mm; W22=222 mm; Wd1=266 mm; Wd2=277 mm; centre=234 mm; dim1=111 mm; nut_dim=123 mm; sweep=30 mm  [stored 0.0984252 ft]; sweep/2=6 mm  [stored 0.019685 ft]; sweep1=13 mm  [stored 0.0426509 ft]; sweep_2=6 mm  [stored 0.019685 ft]; sweep_D=25 mm  [stored 0.082021 ft]; sweep_H=340 mm; sweep_H1=66 mm; sweep_box1=39 mm  [stored 0.127953 ft]; sweep_box2=16 mm  [stored 0.0524934 ft]
- DN300_PN16_Pilot range ( 1,5 - 6): Actuator_L=125 mm; Actuator_L1=112 mm; Actuator_d=68 mm; Body_H=246 mm; Body_Rib_L=103 mm; Bolt_Dia=33 mm; Bonnet_D=123 mm; Bonnet_D1=246 mm; Bonnet_R=258 mm; Bonnet_dia=277 mm; Bonnet_dim1=172 mm; Bonnet_dim1_H=47 mm; Bonnet_dim1_H1=374 mm; Bonnet_dim2=86 mm; Bonnet_dim3=65 mm; Bore=150 mm; Bore1=180 mm; Bore2=240 mm; Centre_D=60 mm; Centre_D1=48 mm; Centre_nut=45 mm; Conrol_dim.=146 mm; Control_dim1=26 mm; Control_dim2=77 mm; Control_dim3=13 mm  [stored 0.0426509 ft]; Control_dim4=221 mm; Control_dim5=35 mm  [stored 0.114829 ft]; Control_dim6=42 mm; Control_dim7=56 mm; D=205 mm; DN=301 mm; FL_T=25 mm  [stored 0.082021 ft]; H3=728 mm; H33=45 mm; H4=89 mm; L=850 mm; L3=284 mm; Nut_Dim1=42 mm; Nut_Dim2=10 mm  [stored 0.0328084 ft]; Nut_T=20 mm  [stored 0.0656168 ft]; Raised_R=22 mm  [stored 0.0721785 ft]; Raised_dis=4 mm  [stored 0.0131234 ft]; Sweep_R=19 mm  [stored 0.062336 ft]; Thickness=15 mm  [stored 0.0492126 ft]; Thickness1=18 mm  [stored 0.0590551 ft]; W=265 mm; W1=277 mm; W11=202 mm; W2=277 mm; W22=222 mm; Wd1=266 mm; Wd2=277 mm; centre=234 mm; dim1=111 mm; nut_dim=123 mm; sweep=30 mm  [stored 0.0984252 ft]; sweep/2=6 mm  [stored 0.019685 ft]; sweep1=13 mm  [stored 0.0426509 ft]; sweep_2=6 mm  [stored 0.019685 ft]; sweep_D=25 mm  [stored 0.082021 ft]; sweep_H=340 mm; sweep_H1=66 mm; sweep_box1=39 mm  [stored 0.127953 ft]; sweep_box2=16 mm  [stored 0.0524934 ft]
- DN300_PN16_Pilot range ( 5 - 11): Actuator_L=125 mm; Actuator_L1=112 mm; Actuator_d=68 mm; Body_H=246 mm; Body_Rib_L=103 mm; Bolt_Dia=33 mm; Bonnet_D=123 mm; Bonnet_D1=246 mm; Bonnet_R=258 mm; Bonnet_dia=277 mm; Bonnet_dim1=172 mm; Bonnet_dim1_H=47 mm; Bonnet_dim1_H1=374 mm; Bonnet_dim2=86 mm; Bonnet_dim3=65 mm; Bore=150 mm; Bore1=180 mm; Bore2=241 mm; Centre_D=60 mm; Centre_D1=48 mm; Centre_nut=45 mm; Conrol_dim.=146 mm; Control_dim1=26 mm; Control_dim2=77 mm; Control_dim3=13 mm  [stored 0.0426509 ft]; Control_dim4=221 mm; Control_dim5=35 mm  [stored 0.114829 ft]; Control_dim6=42 mm; Control_dim7=56 mm; D=205 mm; DN=301 mm; FL_T=25 mm  [stored 0.082021 ft]; H3=728 mm; H33=45 mm; H4=89 mm; L=850 mm; L3=284 mm; Nut_Dim1=42 mm; Nut_Dim2=10 mm  [stored 0.0328084 ft]; Nut_T=20 mm  [stored 0.0656168 ft]; Raised_R=22 mm  [stored 0.0721785 ft]; Raised_dis=4 mm  [stored 0.0131234 ft]; Sweep_R=19 mm  [stored 0.062336 ft]; Thickness=15 mm  [stored 0.0492126 ft]; Thickness1=18 mm  [stored 0.0590551 ft]; W=265 mm; W1=277 mm; W11=202 mm; W2=277 mm; W22=222 mm; Wd1=266 mm; Wd2=277 mm; centre=235 mm; dim1=111 mm; nut_dim=123 mm; sweep=30 mm  [stored 0.0984252 ft]; sweep/2=6 mm  [stored 0.019685 ft]; sweep1=13 mm  [stored 0.0426509 ft]; sweep_2=6 mm  [stored 0.019685 ft]; sweep_D=25 mm  [stored 0.082021 ft]; sweep_H=340 mm; sweep_H1=66 mm; sweep_box1=39 mm  [stored 0.127953 ft]; sweep_box2=16 mm  [stored 0.0524934 ft]
- DN300_PN16_Pilot range ( 10 - 16): Actuator_L=114 mm; Actuator_L1=103 mm; Actuator_d=59 mm; Body_H=213 mm; Body_Rib_L=89 mm; Bolt_Dia=26 mm; Bonnet_D=107 mm; Bonnet_D1=213 mm; Bonnet_R=224 mm; Bonnet_dia=254 mm; Bonnet_dim1=149 mm; Bonnet_dim1_H=47 mm; Bonnet_dim1_H1=339 mm; Bonnet_dim2=75 mm; Bonnet_dim3=56 mm; Bore=125 mm; Bore1=150 mm; Bore2=200 mm; Centre_D=50 mm; Centre_D1=40 mm  [stored 0.131234 ft]; Centre_nut=38 mm; Conrol_dim.=127 mm; Control_dim1=22 mm  [stored 0.0721785 ft]; Control_dim2=67 mm; Control_dim3=11 mm  [stored 0.0360892 ft]; Control_dim4=192 mm; Control_dim5=30 mm  [stored 0.0984252 ft]; Control_dim6=36 mm  [stored 0.11811 ft]; Control_dim7=49 mm; D=178 mm; DN=251 mm; FL_T=22 mm  [stored 0.0721785 ft]; H3=651 mm; H33=40 mm  [stored 0.131234 ft]; H4=81 mm; L=730 mm; L3=246 mm; Nut_Dim1=34 mm; Nut_Dim2=9 mm  [stored 0.0295276 ft]; Nut_T=18 mm  [stored 0.0590551 ft]; Raised_R=21 mm  [stored 0.0688976 ft]; Raised_dis=3 mm  [stored 0.00984252 ft]; Sweep_R=15 mm  [stored 0.0492126 ft]; Thickness=13 mm  [stored 0.0426509 ft]; Thickness1=16 mm  [stored 0.0524934 ft]; W=244 mm; W1=254 mm; W11=187 mm; W2=254 mm; W22=203 mm; Wd1=244 mm; Wd2=254 mm; centre=195 mm; dim1=102 mm; nut_dim=107 mm; sweep=24 mm  [stored 0.0787402 ft]; sweep/2=5 mm  [stored 0.0164042 ft]; sweep1=10 mm  [stored 0.0328084 ft]; sweep_2=5 mm  [stored 0.0164042 ft]; sweep_D=20 mm  [stored 0.0656168 ft]; sweep_H=308 mm; sweep_H1=66 mm; sweep_box1=33 mm; sweep_box2=13 mm  [stored 0.0426509 ft]

note: [stored X ft] marks values corroborated as IEEE doubles in the binary element streams (Revit-internal decimal feet)

## geometry (parser evidence)
native form markers: Sweep x7
no freeform markers — native parametric forms only
